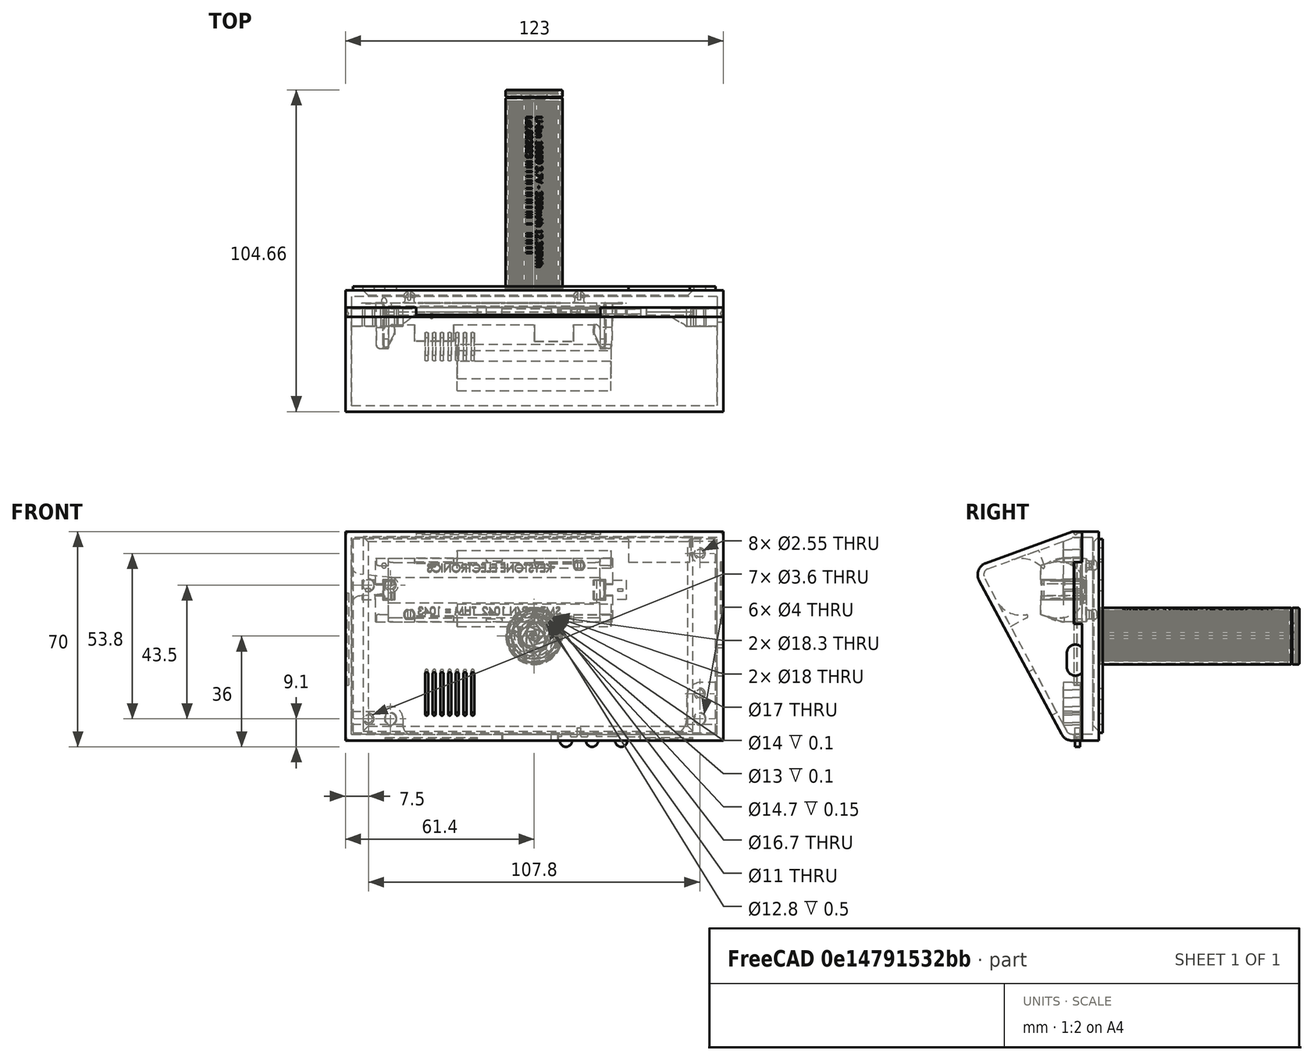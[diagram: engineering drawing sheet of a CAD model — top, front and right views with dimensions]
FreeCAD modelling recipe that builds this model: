
FCSTD DOCUMENT  (FreeCAD 1.0R39285 (Git))
Label: WeatherStation
License: All rights reserved
LicenseURL: https://en.wikipedia.org/wiki/All_rights_reserved
objects: Part::Feature×82, Sketcher::SketchObject×23, PartDesign::Pad×17, PartDesign::Pocket×8, App::Part×3, PartDesign::Body×3, Mesh::Feature×2, Image::ImagePlane×1, PartDesign::SubShapeBinder×1, PartDesign::LinearPattern×1, PartDesign::Fillet×1, PartDesign::Chamfer×1
note: 215 computed .brp shape members not serialized (recipe doc carries the construction recipe); baked Part::Feature solids carry a one-line shape summary decoded from their .brp

FEATURE [Part::Feature] Part__Feature  label="LiLyGO T5-4.7 inch S3 E-paper"
  shape: bbox 118.4 x 6.142 x 63.4 mm, 1563 faces, 0 solids (baked)
FEATURE [Part::Feature] Part__Feature001  label="LiLyGO T5-4.7 inch S3 E-paper001"
  shape: bbox 7.901 x 3.961 x 8.941 mm, 399 faces, 0 solids (baked)
FEATURE [Part::Feature] Part__Feature002  label="LiLyGO T5-4.7 inch S3 E-paper002"
  shape: bbox 10 x 5.45 x 6.416 mm, 158 faces, 0 solids (baked)
FEATURE [Part::Feature] Part__Feature003  label="LiLyGO T5-4.7 inch S3 E-paper003"
  shape: bbox 10 x 5.45 x 6.416 mm, 158 faces, 0 solids (baked)
FEATURE [Part::Feature] Part__Feature004  label="LiLyGO T5-4.7 inch S3 E-paper004"
  shape: bbox 18 x 0.818 x 25.5 mm, 129 faces, 0 solids (baked)
FEATURE [Part::Feature] Part__Feature005  label="LiLyGO T5-4.7 inch S3 E-paper005"
  shape: bbox 15.8 x 2.3 x 17.6 mm, 847 faces, 0 solids (baked)
FEATURE [Part::Feature] Part__Feature006  label="LiLyGO T5-4.7 inch S3 E-paper006"
  shape: bbox 0.9 x 0.018 x 0.9 mm, 6 faces, 0 solids (baked)
FEATURE [Part::Feature] Part__Feature007  label="LiLyGO T5-4.7 inch S3 E-paper007"
  shape: bbox 0.9 x 0.018 x 0.9 mm, 6 faces, 0 solids (baked)
FEATURE [Part::Feature] Part__Feature008  label="LiLyGO T5-4.7 inch S3 E-paper008"
  shape: bbox 0.9 x 0.018 x 0.9 mm, 6 faces, 0 solids (baked)
FEATURE [Part::Feature] Part__Feature009  label="LiLyGO T5-4.7 inch S3 E-paper009"
  shape: bbox 0.9 x 0.018 x 0.9 mm, 6 faces, 0 solids (baked)
FEATURE [Part::Feature] Part__Feature010  label="LiLyGO T5-4.7 inch S3 E-paper010"
  shape: bbox 0.9 x 0.018 x 0.9 mm, 6 faces, 0 solids (baked)
FEATURE [Part::Feature] Part__Feature011  label="LiLyGO T5-4.7 inch S3 E-paper011"
  shape: bbox 0.9 x 0.018 x 0.9 mm, 6 faces, 0 solids (baked)
FEATURE [Part::Feature] Part__Feature012  label="LiLyGO T5-4.7 inch S3 E-paper012"
  shape: bbox 0.9 x 0.018 x 0.9 mm, 6 faces, 0 solids (baked)
FEATURE [Part::Feature] Part__Feature013  label="LiLyGO T5-4.7 inch S3 E-paper013"
  shape: bbox 0.9 x 0.018 x 0.9 mm, 6 faces, 0 solids (baked)
FEATURE [Part::Feature] Part__Feature014  label="LiLyGO T5-4.7 inch S3 E-paper014"
  shape: bbox 0.9 x 0.018 x 0.9 mm, 6 faces, 0 solids (baked)
FEATURE [Part::Feature] Part__Feature015  label="LiLyGO T5-4.7 inch S3 E-paper015"
  shape: bbox 0.868 x 0.836 x 0.9 mm, 16 faces, 0 solids (baked)
FEATURE [Part::Feature] Part__Feature016  label="LiLyGO T5-4.7 inch S3 E-paper016"
  shape: bbox 0.868 x 0.836 x 0.9 mm, 16 faces, 0 solids (baked)
FEATURE [Part::Feature] Part__Feature017  label="LiLyGO T5-4.7 inch S3 E-paper017"
  shape: bbox 0.868 x 0.836 x 0.9 mm, 16 faces, 0 solids (baked)
FEATURE [Part::Feature] Part__Feature018  label="LiLyGO T5-4.7 inch S3 E-paper018"
  shape: bbox 0.868 x 0.836 x 0.9 mm, 16 faces, 0 solids (baked)
FEATURE [Part::Feature] Part__Feature019  label="LiLyGO T5-4.7 inch S3 E-paper019"
  shape: bbox 0.868 x 0.836 x 0.9 mm, 16 faces, 0 solids (baked)
FEATURE [Part::Feature] Part__Feature020  label="LiLyGO T5-4.7 inch S3 E-paper020"
  shape: bbox 0.868 x 0.836 x 0.9 mm, 16 faces, 0 solids (baked)
FEATURE [Part::Feature] Part__Feature021  label="LiLyGO T5-4.7 inch S3 E-paper021"
  shape: bbox 0.868 x 0.836 x 0.9 mm, 16 faces, 0 solids (baked)
FEATURE [Part::Feature] Part__Feature022  label="LiLyGO T5-4.7 inch S3 E-paper022"
  shape: bbox 0.868 x 0.836 x 0.9 mm, 16 faces, 0 solids (baked)
FEATURE [Part::Feature] Part__Feature023  label="LiLyGO T5-4.7 inch S3 E-paper023"
  shape: bbox 0.868 x 0.836 x 0.9 mm, 16 faces, 0 solids (baked)
FEATURE [Part::Feature] Part__Feature024  label="LiLyGO T5-4.7 inch S3 E-paper024"
  shape: bbox 0.868 x 0.836 x 0.9 mm, 16 faces, 0 solids (baked)
FEATURE [Part::Feature] Part__Feature025  label="LiLyGO T5-4.7 inch S3 E-paper025"
  shape: bbox 0.868 x 0.836 x 0.9 mm, 16 faces, 0 solids (baked)
FEATURE [Part::Feature] Part__Feature026  label="LiLyGO T5-4.7 inch S3 E-paper026"
  shape: bbox 0.868 x 0.836 x 0.9 mm, 16 faces, 0 solids (baked)
FEATURE [Part::Feature] Part__Feature027  label="LiLyGO T5-4.7 inch S3 E-paper027"
  shape: bbox 0.868 x 0.836 x 0.9 mm, 16 faces, 0 solids (baked)
FEATURE [Part::Feature] Part__Feature028  label="LiLyGO T5-4.7 inch S3 E-paper028"
  shape: bbox 0.868 x 0.836 x 0.9 mm, 16 faces, 0 solids (baked)
FEATURE [Part::Feature] Part__Feature029  label="LiLyGO T5-4.7 inch S3 E-paper029"
  shape: bbox 0.868 x 0.836 x 0.9 mm, 16 faces, 0 solids (baked)
FEATURE [Part::Feature] Part__Feature030  label="LiLyGO T5-4.7 inch S3 E-paper030"
  shape: bbox 0.868 x 0.836 x 0.9 mm, 16 faces, 0 solids (baked)
FEATURE [Part::Feature] Part__Feature031  label="LiLyGO T5-4.7 inch S3 E-paper031"
  shape: bbox 0.868 x 0.836 x 0.9 mm, 16 faces, 0 solids (baked)
FEATURE [Part::Feature] Part__Feature032  label="LiLyGO T5-4.7 inch S3 E-paper032"
  shape: bbox 0.868 x 0.836 x 0.9 mm, 16 faces, 0 solids (baked)
FEATURE [Part::Feature] Part__Feature033  label="LiLyGO T5-4.7 inch S3 E-paper033"
  shape: bbox 0.868 x 0.836 x 0.9 mm, 16 faces, 0 solids (baked)
FEATURE [Part::Feature] Part__Feature034  label="LiLyGO T5-4.7 inch S3 E-paper034"
  shape: bbox 0.868 x 0.836 x 0.9 mm, 16 faces, 0 solids (baked)
FEATURE [Part::Feature] Part__Feature035  label="LiLyGO T5-4.7 inch S3 E-paper035"
  shape: bbox 0.868 x 0.836 x 0.9 mm, 16 faces, 0 solids (baked)
FEATURE [Part::Feature] Part__Feature036  label="LiLyGO T5-4.7 inch S3 E-paper036"
  shape: bbox 0.868 x 0.836 x 0.9 mm, 16 faces, 0 solids (baked)
FEATURE [Part::Feature] Part__Feature037  label="LiLyGO T5-4.7 inch S3 E-paper037"
  shape: bbox 0.868 x 0.836 x 0.9 mm, 16 faces, 0 solids (baked)
FEATURE [Part::Feature] Part__Feature038  label="LiLyGO T5-4.7 inch S3 E-paper038"
  shape: bbox 0.868 x 0.836 x 0.9 mm, 16 faces, 0 solids (baked)
FEATURE [Part::Feature] Part__Feature039  label="LiLyGO T5-4.7 inch S3 E-paper039"
  shape: bbox 0.868 x 0.836 x 0.9 mm, 16 faces, 0 solids (baked)
FEATURE [Part::Feature] Part__Feature040  label="LiLyGO T5-4.7 inch S3 E-paper040"
  shape: bbox 0.868 x 0.836 x 0.9 mm, 16 faces, 0 solids (baked)
FEATURE [Part::Feature] Part__Feature041  label="LiLyGO T5-4.7 inch S3 E-paper041"
  shape: bbox 0.868 x 0.836 x 0.9 mm, 16 faces, 0 solids (baked)
FEATURE [Part::Feature] Part__Feature042  label="LiLyGO T5-4.7 inch S3 E-paper042"
  shape: bbox 0.868 x 0.836 x 0.9 mm, 16 faces, 0 solids (baked)
FEATURE [Part::Feature] Part__Feature043  label="LiLyGO T5-4.7 inch S3 E-paper043"
  shape: bbox 0.9 x 0.836 x 0.868 mm, 16 faces, 0 solids (baked)
FEATURE [Part::Feature] Part__Feature044  label="LiLyGO T5-4.7 inch S3 E-paper044"
  shape: bbox 0.9 x 0.836 x 0.868 mm, 16 faces, 0 solids (baked)
FEATURE [Part::Feature] Part__Feature045  label="LiLyGO T5-4.7 inch S3 E-paper045"
  shape: bbox 0.9 x 0.836 x 0.868 mm, 16 faces, 0 solids (baked)
FEATURE [Part::Feature] Part__Feature046  label="LiLyGO T5-4.7 inch S3 E-paper046"
  shape: bbox 0.9 x 0.836 x 0.868 mm, 16 faces, 0 solids (baked)
FEATURE [Part::Feature] Part__Feature047  label="LiLyGO T5-4.7 inch S3 E-paper047"
  shape: bbox 0.9 x 0.836 x 0.868 mm, 16 faces, 0 solids (baked)
FEATURE [Part::Feature] Part__Feature048  label="LiLyGO T5-4.7 inch S3 E-paper048"
  shape: bbox 0.9 x 0.836 x 0.868 mm, 16 faces, 0 solids (baked)
FEATURE [Part::Feature] Part__Feature049  label="LiLyGO T5-4.7 inch S3 E-paper049"
  shape: bbox 0.9 x 0.836 x 0.868 mm, 16 faces, 0 solids (baked)
FEATURE [Part::Feature] Part__Feature050  label="LiLyGO T5-4.7 inch S3 E-paper050"
  shape: bbox 0.9 x 0.836 x 0.868 mm, 16 faces, 0 solids (baked)
FEATURE [Part::Feature] Part__Feature051  label="LiLyGO T5-4.7 inch S3 E-paper051"
  shape: bbox 0.9 x 0.836 x 0.868 mm, 16 faces, 0 solids (baked)
FEATURE [Part::Feature] Part__Feature052  label="LiLyGO T5-4.7 inch S3 E-paper052"
  shape: bbox 0.9 x 0.836 x 0.868 mm, 16 faces, 0 solids (baked)
FEATURE [Part::Feature] Part__Feature053  label="LiLyGO T5-4.7 inch S3 E-paper053"
  shape: bbox 0.9 x 0.836 x 0.868 mm, 16 faces, 0 solids (baked)
FEATURE [Part::Feature] Part__Feature054  label="LiLyGO T5-4.7 inch S3 E-paper054"
  shape: bbox 0.9 x 0.836 x 0.868 mm, 16 faces, 0 solids (baked)
FEATURE [Part::Feature] Part__Feature055  label="LiLyGO T5-4.7 inch S3 E-paper055"
  shape: bbox 0.8 x 1.034 x 8.828 mm, 98 faces, 0 solids (baked)
FEATURE [Part::Feature] Part__Feature056  label="LiLyGO T5-4.7 inch S3 E-paper056"
  shape: bbox 0.8 x 1.034 x 9.125 mm, 98 faces, 0 solids (baked)
FEATURE [Part::Feature] Part__Feature057  label="LiLyGO T5-4.7 inch S3 E-paper057"
  shape: bbox 0.8 x 1.034 x 8.828 mm, 98 faces, 0 solids (baked)
FEATURE [Part::Feature] Part__Feature058  label="LiLyGO T5-4.7 inch S3 E-paper058"
  shape: bbox 0.8 x 1.053 x 8.525 mm, 98 faces, 0 solids (baked)
FEATURE [Part::Feature] Part__Feature059  label="LiLyGO T5-4.7 inch S3 E-paper059"
  shape: bbox 0.8 x 1.034 x 8.828 mm, 98 faces, 0 solids (baked)
FEATURE [Part::Feature] Part__Feature060  label="LiLyGO T5-4.7 inch S3 E-paper060"
  shape: bbox 0.8 x 1.053 x 8.525 mm, 98 faces, 0 solids (baked)
FEATURE [Part::Feature] Part__Feature061  label="LiLyGO T5-4.7 inch S3 E-paper061"
  shape: bbox 0.8 x 1.034 x 8.828 mm, 98 faces, 0 solids (baked)
FEATURE [Part::Feature] Part__Feature062  label="LiLyGO T5-4.7 inch S3 E-paper062"
  shape: bbox 0.8 x 1.034 x 8.828 mm, 98 faces, 0 solids (baked)
FEATURE [Part::Feature] Part__Feature063  label="LiLyGO T5-4.7 inch S3 E-paper063"
  shape: bbox 4.48 x 1.155 x 14 mm, 148 faces, 0 solids (baked)
FEATURE [Part::Feature] Part__Feature064  label="LiLyGO T5-4.7 inch S3 E-paper064"
  shape: bbox 14.24 x 1.381 x 14.95 mm, 295 faces, 0 solids (baked)
FEATURE [Part::Feature] Part__Feature065  label="LiLyGO T5-4.7 inch S3 E-paper065"
  shape: bbox 2.66 x 1.087 x 9.021 mm, 113 faces, 0 solids (baked)
FEATURE [Part::Feature] Part__Feature066  label="LiLyGO T5-4.7 inch S3 E-paper066"
  shape: bbox 0.5151 x 0.833 x 6.833 mm, 16 faces, 0 solids (baked)
FEATURE [Part::Feature] Part__Feature067  label="LiLyGO T5-4.7 inch S3 E-paper067"
  shape: bbox 14.94 x 1.5 x 14.95 mm, 496 faces, 0 solids (baked)
FEATURE [Part::Feature] Part__Feature068  label="LiLyGO T5-4.7 inch S3 E-paper068"
  shape: bbox 7.5 x 9.25 x 11.5 mm, 87 faces, 0 solids (baked)
FEATURE [Part::Feature] Part__Feature069  label="LiLyGO T5-4.7 inch S3 E-paper069"
  shape: bbox 1.44 x 1.308 x 10.41 mm, 3 faces, 0 solids (baked)
FEATURE [Sketcher::SketchObject] Sketch
  ArcFitTolerance = 1e-06
  AttachmentSupport = -> [XZ_Plane002]
  FullyConstrained = true
  MakeInternals = false
  MapMode = 5
  Placement = pos=(0,0,0) rot=(1,0,0;1.5708rad)
  expr: Constraints[16] = 119 + 2 + 2
  expr: Constraints[17] = 64 + 2 + 2
  sketch-geometry (8):
    g0: LineSegment StartX=61.6 StartY=34 StartZ=0 EndX=-61.4 EndY=34 EndZ=0
    g1: LineSegment StartX=-61.4 StartY=34 StartZ=0 EndX=-61.4 EndY=-34 EndZ=0
    g2: LineSegment StartX=-61.4 StartY=-34 StartZ=0 EndX=61.6 EndY=-34 EndZ=0
    g3: LineSegment StartX=61.6 StartY=-34 StartZ=0 EndX=61.6 EndY=34 EndZ=0
    g4: LineSegment StartX=-54 StartY=-29.3 StartZ=0 EndX=50 EndY=-29.3 EndZ=0
    g5: LineSegment StartX=50 StartY=-29.3 StartZ=0 EndX=50 EndY=30.7 EndZ=0
    g6: LineSegment StartX=50 StartY=30.7 StartZ=0 EndX=-54 EndY=30.7 EndZ=0
    g7: LineSegment StartX=-54 StartY=30.7 StartZ=0 EndX=-54 EndY=-29.3 EndZ=0
  constraints (24):
    c: Coincident(g0,g1)
    c: Coincident(g1,g2)
    c: Coincident(g2,g3)
    c: Coincident(g3,g0)
    c: Horizontal(g0)
    c: Horizontal(g2)
    c: Vertical(g1)
    c: Vertical(g3)
    c: Coincident(g4,g5)
    c: Coincident(g5,g6)
    c: Coincident(g6,g7)
    c: Coincident(g7,g4)
    c: Horizontal(g4)
    c: Horizontal(g6)
    c: Vertical(g5)
    c: Vertical(g7)
    c: DistanceX(g2,g2) = 123
    c: DistanceY(g3,g3) = 68
    c: Distance(g1,g-2) = 61.4
    c: Distance(g-1,g2) = 34
    c: DistanceX(g6,g6) = 104
    c: DistanceY(g5,g5) = 60
    c: DistanceY(g4,g-1) = 29.3
    c: Distance(g4,g-2) = 54
FEATURE [PartDesign::Pad] Pad  label="BeselPad"
  Direction = (0,-1,2e-16)
  Length = 2
  Length2 = 10
  Placement = pos=(0,0,0) rot=(1,0,0;1.5708rad)
  Profile = -> Sketch
  ReferenceAxis = -> Sketch [N_Axis]
  Suppressed = false
  Type = 0
FEATURE [Sketcher::SketchObject] Sketch001
  ArcFitTolerance = 1e-06
  AttachmentSupport = -> [Pad]
  ExternalGeometry = -> [Pad]
  FullyConstrained = true
  MakeInternals = false
  MapMode = 5
  Placement = pos=(0,-2,4e-16) rot=(1,0,0;1.5708rad)
  sketch-geometry (8):
    g0: LineSegment StartX=-61.4 StartY=34 StartZ=0 EndX=-61.4 EndY=-34 EndZ=0
    g1: LineSegment StartX=-61.4 StartY=-34 StartZ=0 EndX=61.6 EndY=-34 EndZ=0
    g2: LineSegment StartX=61.6 StartY=-34 StartZ=0 EndX=61.6 EndY=34 EndZ=0
    g3: LineSegment StartX=61.6 StartY=34 StartZ=0 EndX=-61.4 EndY=34 EndZ=0
    g4: LineSegment StartX=-59.4 StartY=32 StartZ=0 EndX=-59.4 EndY=-32 EndZ=0
    g5: LineSegment StartX=-59.4 StartY=-32 StartZ=0 EndX=59.6 EndY=-32 EndZ=0
    g6: LineSegment StartX=59.6 StartY=-32 StartZ=0 EndX=59.6 EndY=32 EndZ=0
    g7: LineSegment StartX=59.6 StartY=32 StartZ=0 EndX=-59.4 EndY=32 EndZ=0
  constraints (22):
    c: Coincident(g0,g1)
    c: Coincident(g1,g2)
    c: Coincident(g2,g3)
    c: Coincident(g3,g0)
    c: Vertical(g0)
    c: Vertical(g2)
    c: Horizontal(g1)
    c: Horizontal(g3)
    c: Coincident(g0,g-3)
    c: Coincident(g1,g-4)
    c: Coincident(g4,g5)
    c: Coincident(g5,g6)
    c: Coincident(g6,g7)
    c: Coincident(g7,g4)
    c: Vertical(g4)
    c: Vertical(g6)
    c: Horizontal(g5)
    c: Horizontal(g7)
    c: DistanceY(g4,g4) = 64
    c: DistanceX(g5,g5) = 119
    c: Distance(g4,g0) = 2
    c: Distance(g4,g3) = 2
FEATURE [PartDesign::Pad] Pad001  label="SideWallPad"
  BaseFeature = -> Pad
  Direction = (0,-1,2e-16)
  Length = 3.5
  Length2 = 10
  Placement = pos=(0,0,0) rot=(1,0,0;1.5708rad)
  Profile = -> Sketch001
  ReferenceAxis = -> Sketch001 [N_Axis]
  Suppressed = false
  Type = 0
FEATURE [Part::Feature] Part__Feature070  label="Li-Ion_18650_cell"
  shape: bbox 19.81 x 65.04 x 19.81 mm, 31 faces (baked)
FEATURE [Part::Feature] Part__Feature071  label="Li-Ion_18650_cell001"
  shape: bbox 17.9 x 0.5 x 17.9 mm, 4 faces (baked)
FEATURE [Part::Feature] Part__Feature072  label="Li-Ion_18650_cell002"
  shape: bbox 17.52 x 3.32 x 17.52 mm, 44 faces (baked)
FEATURE [Part::Feature] Part__Feature073  label="Li-Ion_18650_cell003"
  shape: bbox 16.4 x 61 x 16.35 mm, 6 faces (baked)
FEATURE [Part::Feature] Part__Feature074  label="Li-Ion_18650_cell004"
  shape: bbox 16.7 x 61 x 16.66 mm, 6 faces (baked)
FEATURE [Part::Feature] Part__Feature075  label="Li-Ion_18650_cell005"
  shape: bbox 17.01 x 61 x 16.97 mm, 6 faces (baked)
FEATURE [Part::Feature] Part__Feature076  label="Li-Ion_18650_cell006"
  shape: bbox 17.13 x 0.2387 x 17.13 mm, 3 faces (baked)
FEATURE [Part::Feature] Part__Feature077  label="Li-Ion_18650_cell007"
  shape: bbox 16.02 x 0.1534 x 16.02 mm, 3 faces (baked)
FEATURE [Part::Feature] Part__Feature078  label="Li-Ion_18650_cell008"
  shape: bbox 17.91 x 61.47 x 17.91 mm, 4 faces (baked)
FEATURE [Part::Feature] Part__Feature079  label="Li-Ion_18650_cell009"
  shape: bbox 17.7 x 0.1 x 17.7 mm, 4 faces (baked)
FEATURE [Part::Feature] Part__Feature080  label="Li-Ion_18650_cell010"
  shape: bbox 20.03 x 65.36 x 141.7 mm, 778 faces (baked)
FEATURE [App::Part] Li_Ion_18650_cell  label="Li-Ion_18650_cell011"
  Group = -> [Part__Feature070,Part__Feature071,Part__Feature072,Part__Feature073,Part__Feature074,Part__Feature075,Part__Feature076,Part__Feature077,Part__Feature078,Part__Feature079,Part__Feature080]
  Origin = -> Origin004
  Placement = pos=(-32.5,-18.75,15.75) rot=(0,0,1;4.71239rad)
FEATURE [Part::Feature] Part__Feature081  label="keystone-PN1042"
  Placement = pos=(-13,-4,15) rot=(-0.707107,0,0.707107;3.14159rad)
  shape: bbox 86.01 x 18.29 x 20.82 mm, 683 faces (baked)
FEATURE [Mesh::Feature] a  label="RefShell_back"
  Placement = pos=(-9e-16,7.25,0) rot=(1,0,0;3.14159rad)
FEATURE [Image::ImagePlane] LILYGO_T5_E_PAPER_1  label="LILYGO-T5-E-PAPER_1"
  Placement = pos=(0,0,0) rot=(1,0,0;1.5708rad)
  XSize = 163.006
  YSize = 89.7063
FEATURE [Sketcher::SketchObject] Sketch007
  ArcFitTolerance = 1e-06
  AttachmentSupport = -> [XZ_Plane005]
  FullyConstrained = true
  MakeInternals = false
  MapMode = 5
  Placement = pos=(0,0,0) rot=(1,0,0;1.5708rad)
  sketch-geometry (15):
    g0: LineSegment StartX=-59 StartY=31.5 StartZ=0 EndX=-59 EndY=-31.5 EndZ=0
    g1: LineSegment StartX=-59 StartY=-31.5 StartZ=0 EndX=59 EndY=-31.5 EndZ=0
    g2: LineSegment StartX=59 StartY=-31.5 StartZ=0 EndX=59 EndY=31.5 EndZ=0
    g3: LineSegment StartX=59 StartY=31.5 StartZ=0 EndX=50.7 EndY=31.5 EndZ=0
    g4: LineSegment StartX=30.7 StartY=31.5 StartZ=0 EndX=30.7 EndY=24.1 EndZ=0
    g5: LineSegment StartX=30.7 StartY=24.1 StartZ=0 EndX=50.7 EndY=24.1 EndZ=0
    g6: LineSegment StartX=50.7 StartY=24.1 StartZ=0 EndX=50.7 EndY=31.5 EndZ=0
    g7: LineSegment StartX=30.7 StartY=31.5 StartZ=0 EndX=-59 EndY=31.5 EndZ=0
    g8: Circle CenterX=53.9 CenterY=26.9 CenterZ=0 NormalX=0 NormalY=0 NormalZ=1 AngleXU=0 Radius=1.8
    g9: Circle CenterX=53.9 CenterY=-18.7 CenterZ=0 NormalX=0 NormalY=0 NormalZ=1 AngleXU=0 Radius=1.8
    g10: Circle CenterX=53.9 CenterY=-26.9 CenterZ=0 NormalX=0 NormalY=0 NormalZ=1 AngleXU=0 Radius=1.8
    g11: Circle CenterX=-53.9 CenterY=-26.9 CenterZ=0 NormalX=0 NormalY=0 NormalZ=1 AngleXU=0 Radius=1.8
    g12: Circle CenterX=-46.7 CenterY=-26.9 CenterZ=0 NormalX=0 NormalY=0 NormalZ=1 AngleXU=0 Radius=1.8
    g13: Circle CenterX=-53.9 CenterY=16.6 CenterZ=0 NormalX=0 NormalY=0 NormalZ=1 AngleXU=0 Radius=1.8
    g14: Circle CenterX=-46.7 CenterY=16.6 CenterZ=0 NormalX=0 NormalY=0 NormalZ=1 AngleXU=0 Radius=1.8
  constraints (45):
    c: Coincident(g0,g1)
    c: Coincident(g1,g2)
    c: Coincident(g2,g3)
    c: Coincident(g7,g0)
    c: Vertical(g0)
    c: Vertical(g2)
    c: Horizontal(g1)
    c: Horizontal(g3)
    c: Distance(g0,g2) = 118
    c: Distance(g1,g7) = 63
    c: DistanceY(g-1,g2) = 31.5
    c: DistanceX(g-1,g2) = 59
    c: Coincident(g4,g5)
    c: Coincident(g5,g6)
    c: Horizontal(g5)
    c: Vertical(g4)
    c: Vertical(g6)
    c: Horizontal(g4,g3)
    c: DistanceY(g4,g4) = 7.4
    c: DistanceX(g5,g5) = 20
    c: DistanceX(g3,g3) = 8.3
    c: Coincident(g6,g3)
    c: Horizontal(g7)
    c: Coincident(g4,g7)
    c: Equal(g13,g14)
    c: Equal(g14,g11)
    c: Equal(g11,g12)
    c: Equal(g12,g10)
    c: Equal(g10,g9)
    c: Equal(g9,g8)
    c: Diameter(g8) = 3.6
    c: Horizontal(g13,g14)
    c: Horizontal(g11,g12)
    c: Horizontal(g12,g10)
    c: Vertical(g8,g9)
    c: Vertical(g9,g10)
    c: Distance(g11,g1) = 2.8
    c: Distance(g11,g0) = 3.3
    c: Vertical(g11,g13)
    c: Vertical(g12,g14)
    c: Distance(g12,g0) = 10.5
    c: Distance(g13,g7) = 13.1
    c: Distance(g10,g2) = 3.3
    c: Distance(g9,g1) = 11
    c: Distance(g8,g3) = 2.8
FEATURE [PartDesign::Pad] Pad005
  Direction = (0,-1,2e-16)
  Length = 1.2
  Length2 = 10
  Placement = pos=(0,0,0) rot=(1,0,0;1.5708rad)
  Profile = -> Sketch007
  ReferenceAxis = -> Sketch007 [N_Axis]
  Suppressed = false
  Type = 0
FEATURE [PartDesign::Body] Body002  label="PCB"
  AllowCompound = false
  Group = -> [Sketch007,Pad005]
  Origin = -> Origin005
  Placement = pos=(0,1.25,0) rot=(0,0,1;0rad)
  Tip = -> Pad005
FEATURE [App::Part] LiLyGO_T5_4_7_inch_S3_E_paper  label="LiLyGO T5-4.7 inch S3 E-paper070"
  Group = -> [Part__Feature,Part__Feature001,Part__Feature002,Part__Feature003,Part__Feature004,Part__Feature005,Part__Feature006,Part__Feature007,Part__Feature008,Part__Feature009,Part__Feature010,Part__Feature011,Part__Feature012,Part__Feature013,Part__Feature014,Part__Feature015,Part__Feature016,Part__Feature017,Part__Feature018,Part__Feature019,Part__Feature020,Part__Feature021,Part__Feature022,+49 more]
  Origin = -> Origin
FEATURE [Mesh::Feature] b
  Placement = pos=(0,7.25,-9e-16) rot=(1,0,0;3.14159rad)
FEATURE [Sketcher::SketchObject] Sketch008
  ArcFitTolerance = 1e-06
  AttachmentSupport = -> [Pad001]
  ExternalGeometry = -> [Pad001]
  FullyConstrained = true
  MakeInternals = false
  MapMode = 5
  Placement = pos=(61.6,0,0) rot=(0.707107,0,0.707107;3.14159rad)
  sketch-geometry (5):
    g0: LineSegment StartX=34 StartY=5.5 StartZ=0 EndX=34 EndY=8 EndZ=0
    g1: LineSegment StartX=33.5 StartY=5.5 StartZ=0 EndX=33.5 EndY=7 EndZ=0
    g2: ArcOfCircle CenterX=33.5 CenterY=7.5 CenterZ=0 NormalX=0 NormalY=0 NormalZ=1 AngleXU=0 Radius=0.5 StartAngle=1.5708 EndAngle=4.71239
    g3: LineSegment StartX=33.5 StartY=8 StartZ=0 EndX=34 EndY=8 EndZ=0
    g4: LineSegment StartX=33.5 StartY=5.5 StartZ=0 EndX=34 EndY=5.5 EndZ=0
  constraints (15):
    c: Coincident(g0,g-4)
    c: Vertical(g0)
    c: PointOnObject(g1,g-7)
    c: Vertical(g1)
    c: Coincident(g2,g1)
    c: Coincident(g3,g2)
    c: Coincident(g3,g0)
    c: Horizontal(g3)
    c: Radius(g2) = 0.5
    c: Distance(g3,g3) = 0.5
    c: DistanceY(g0,g0) = 2.5
    c: Vertical(g1,g2)
    c: Vertical(g2,g2)
    c: Coincident(g4,g1)
    c: Coincident(g4,g0)
FEATURE [PartDesign::Pad] Pad006  label="BotTabPad"
  BaseFeature = -> Pad001
  Direction = (1,0,-2e-16)
  Length = 100
  Length2 = -40
  Placement = pos=(0,0,0) rot=(1,0,0;1.5708rad)
  Profile = -> Sketch008
  ReferenceAxis = -> Sketch008 [N_Axis]
  Reversed = true
  Suppressed = false
  Type = 4
FEATURE [Sketcher::SketchObject] Sketch009
  ArcFitTolerance = 1e-06
  AttachmentSupport = -> [Pad006]
  ExternalGeometry = -> [Pad006]
  FullyConstrained = true
  MakeInternals = false
  MapMode = 5
  Placement = pos=(0,1.5e-14,34) rot=(0,0,1;3.14159rad)
  sketch-geometry (5):
    g0: LineSegment StartX=-61.1 StartY=5.5 StartZ=0 EndX=-61.6 EndY=5.5 EndZ=0
    g1: LineSegment StartX=-61.6 StartY=5.5 StartZ=0 EndX=-61.6 EndY=8 EndZ=0
    g2: LineSegment StartX=-61.6 StartY=8 StartZ=0 EndX=-61.1 EndY=8 EndZ=0
    g3: LineSegment StartX=-61.1 StartY=5.5 StartZ=0 EndX=-61.1 EndY=7 EndZ=0
    g4: ArcOfCircle CenterX=-61.1 CenterY=7.5 CenterZ=0 NormalX=0 NormalY=0 NormalZ=1 AngleXU=0 Radius=0.5 StartAngle=4.71239 EndAngle=7.85398
  constraints (15):
    c: PointOnObject(g0,g-3)
    c: Coincident(g0,g-3)
    c: Coincident(g1,g0)
    c: Vertical(g1)
    c: Coincident(g2,g1)
    c: Horizontal(g2)
    c: Coincident(g3,g0)
    c: Vertical(g3)
    c: Coincident(g4,g3)
    c: Coincident(g4,g2)
    c: Vertical(g2,g4)
    c: Vertical(g4,g3)
    c: DistanceX(g2,g2) = 0.5
    c: Radius(g4) = 0.5
    c: DistanceY(g1,g1) = 2.5
FEATURE [PartDesign::Pad] Pad007  label="RightTabPad"
  BaseFeature = -> Pad006
  Direction = (0,0,1)
  Length = 30
  Length2 = -10
  Placement = pos=(0,0,0) rot=(1,0,0;1.5708rad)
  Profile = -> Sketch009
  ReferenceAxis = -> Sketch009 [N_Axis]
  Reversed = true
  Suppressed = false
  Type = 4
FEATURE [Sketcher::SketchObject] Sketch010
  ArcFitTolerance = 1e-06
  AttachmentSupport = -> [Pad007]
  ExternalGeometry = -> [Pad007]
  FullyConstrained = true
  MakeInternals = false
  MapMode = 5
  Placement = pos=(0,1.5e-14,34) rot=(0,0,1;3.14159rad)
  sketch-geometry (5):
    g0: LineSegment StartX=60.9 StartY=7 StartZ=0 EndX=60.9 EndY=5.5 EndZ=0
    g1: LineSegment StartX=60.9 StartY=5.5 StartZ=0 EndX=61.4 EndY=5.5 EndZ=0
    g2: LineSegment StartX=61.4 StartY=5.5 StartZ=0 EndX=61.4 EndY=8 EndZ=0
    g3: LineSegment StartX=61.4 StartY=8 StartZ=0 EndX=60.9 EndY=8 EndZ=0
    g4: ArcOfCircle CenterX=60.9 CenterY=7.5 CenterZ=0 NormalX=0 NormalY=0 NormalZ=1 AngleXU=0 Radius=0.5 StartAngle=1.5708 EndAngle=4.71239
  constraints (15):
    c: PointOnObject(g0,g-4)
    c: Vertical(g0)
    c: Coincident(g0,g1)
    c: Coincident(g1,g-4)
    c: Coincident(g1,g2)
    c: Vertical(g2)
    c: Coincident(g2,g3)
    c: Horizontal(g3)
    c: Coincident(g4,g0)
    c: Coincident(g4,g3)
    c: DistanceX(g3,g3) = 0.5
    c: Vertical(g4,g3)
    c: Vertical(g3,g0)
    c: Radius(g4) = 0.5
    c: DistanceY(g2,g2) = 2.5
FEATURE [PartDesign::Pad] Pad008  label="LeftTabPad"
  BaseFeature = -> Pad007
  Direction = (0,0,1)
  Length = 50
  Length2 = -20
  Placement = pos=(0,0,0) rot=(1,0,0;1.5708rad)
  Profile = -> Sketch010
  ReferenceAxis = -> Sketch010 [N_Axis]
  Reversed = true
  Suppressed = false
  Type = 4
FEATURE [Sketcher::SketchObject] Sketch011
  ArcFitTolerance = 1e-06
  AttachmentSupport = -> [Pad008]
  ExternalGeometry = -> [Pad008]
  FullyConstrained = true
  MakeInternals = false
  MapMode = 5
  Placement = pos=(61.6,0,0) rot=(0.707107,0,0.707107;3.14159rad)
  sketch-geometry (5):
    g0: LineSegment StartX=-33.5 StartY=7 StartZ=0 EndX=-33.5 EndY=5.5 EndZ=0
    g1: LineSegment StartX=-33.5 StartY=5.5 StartZ=0 EndX=-34 EndY=5.5 EndZ=0
    g2: LineSegment StartX=-34 StartY=5.5 StartZ=0 EndX=-34 EndY=8 EndZ=0
    g3: LineSegment StartX=-34 StartY=8 StartZ=0 EndX=-33.5 EndY=8 EndZ=0
    g4: ArcOfCircle CenterX=-33.5 CenterY=7.5 CenterZ=0 NormalX=0 NormalY=0 NormalZ=1 AngleXU=0 Radius=0.5 StartAngle=4.71239 EndAngle=7.85398
  constraints (15):
    c: PointOnObject(g0,g-3)
    c: Vertical(g0)
    c: Coincident(g0,g1)
    c: Coincident(g1,g-3)
    c: Coincident(g1,g2)
    c: Vertical(g2)
    c: Coincident(g2,g3)
    c: Horizontal(g3)
    c: Coincident(g4,g3)
    c: Coincident(g4,g0)
    c: DistanceX(g3,g3) = 0.5
    c: Radius(g4) = 0.5
    c: DistanceY(g2,g2) = 2.5
    c: Vertical(g0,g4)
    c: Vertical(g4,g3)
FEATURE [PartDesign::Pad] Pad009  label="Top1TabPad"
  BaseFeature = -> Pad008
  Direction = (1,0,-2e-16)
  Length = 25
  Length2 = -10
  Placement = pos=(0,0,0) rot=(1,0,0;1.5708rad)
  Profile = -> Sketch011
  ReferenceAxis = -> Sketch011 [N_Axis]
  Reversed = true
  Suppressed = false
  Type = 4
FEATURE [PartDesign::Pad] Pad010  label="Top2TabPad"
  BaseFeature = -> Pad009
  Direction = (1,0,-2e-16)
  Length = 110
  Length2 = -80
  Placement = pos=(0,0,0) rot=(1,0,0;1.5708rad)
  Profile = -> Sketch011
  ReferenceAxis = -> Sketch011 [N_Axis]
  Reversed = true
  Suppressed = false
  Type = 4
FEATURE [PartDesign::SubShapeBinder] Binder
  BindCopyOnChange = 0
  BindMode = 0
  ClaimChildren = false
  Context = -> Part [Body003.Binder.]
  Fuse = false
  MakeFace = true
  OffsetFill = false
  OffsetIntersection = false
  OffsetJoinType = 0
  OffsetOpenResult = false
  PartialLoad = false
  Relative = true
  Support = -> [Body[Pad010.Face13]]
  _Version = 2
FEATURE [Sketcher::SketchObject] Sketch012
  ArcFitTolerance = 1e-06
  AttachmentSupport = -> [Binder]
  ExternalGeometry = -> [Binder]
  FullyConstrained = true
  MakeInternals = false
  MapMode = 5
  Placement = pos=(0,-5.5,0) rot=(1,0,0;1.5708rad)
  sketch-geometry (32):
    g0: LineSegment StartX=-59.4 StartY=32 StartZ=0 EndX=-59.4 EndY=-32 EndZ=0
    g1: LineSegment StartX=-59.4 StartY=-32 StartZ=0 EndX=7.6 EndY=-32 EndZ=0
    g2: LineSegment StartX=59.6 StartY=-32 StartZ=0 EndX=59.6 EndY=32 EndZ=0
    g3: LineSegment StartX=59.6 StartY=32 StartZ=0 EndX=-59.4 EndY=32 EndZ=0
    g4: LineSegment StartX=-61.4 StartY=34 StartZ=0 EndX=-38.4 EndY=34 EndZ=0
    g5: LineSegment StartX=-38.4 StartY=34 StartZ=0 EndX=-38.4 EndY=33.5 EndZ=0
    g6: LineSegment StartX=-38.4 StartY=33.5 StartZ=0 EndX=21.6 EndY=33.5 EndZ=0
    g7: LineSegment StartX=21.6 StartY=33.5 StartZ=0 EndX=21.6 EndY=34 EndZ=0
    g8: LineSegment StartX=21.6 StartY=34 StartZ=0 EndX=61.6 EndY=34 EndZ=0
    g9: LineSegment StartX=61.6 StartY=34 StartZ=0 EndX=61.6 EndY=24 EndZ=0
    g10: LineSegment StartX=61.6 StartY=24 StartZ=0 EndX=61.1 EndY=24 EndZ=0
    g11: LineSegment StartX=61.1 StartY=24 StartZ=0 EndX=61.1 EndY=4 EndZ=0
    g12: LineSegment StartX=61.1 StartY=4 StartZ=0 EndX=61.6 EndY=4 EndZ=0
    g13: LineSegment StartX=61.6 StartY=-34 StartZ=0 EndX=51.6 EndY=-34 EndZ=0
    g14: LineSegment StartX=51.6 StartY=-34 StartZ=0 EndX=51.6 EndY=-33.5 EndZ=0
    g15: LineSegment StartX=51.6 StartY=-33.5 StartZ=0 EndX=36.6 EndY=-33.5 EndZ=0
    g16: LineSegment StartX=36.6 StartY=-33.5 StartZ=0 EndX=36.6 EndY=-34 EndZ=0
    g17: LineSegment StartX=-18.4 StartY=-34 StartZ=0 EndX=-18.4 EndY=-33.5 EndZ=0
    g18: LineSegment StartX=-18.4 StartY=-33.5 StartZ=0 EndX=-48.4 EndY=-33.5 EndZ=0
    g19: LineSegment StartX=-48.4 StartY=-33.5 StartZ=0 EndX=-48.4 EndY=-34 EndZ=0
    g20: LineSegment StartX=-48.4 StartY=-34 StartZ=0 EndX=-61.4 EndY=-34 EndZ=0
    g21: LineSegment StartX=-61.4 StartY=-34 StartZ=0 EndX=-61.4 EndY=-16 EndZ=0
    g22: LineSegment StartX=-61.4 StartY=-16 StartZ=0 EndX=-60.9 EndY=-16 EndZ=0
    g23: LineSegment StartX=-60.9 StartY=-16 StartZ=0 EndX=-60.9 EndY=14 EndZ=0
    g24: LineSegment StartX=-60.9 StartY=14 StartZ=0 EndX=-61.4 EndY=14 EndZ=0
    g25: LineSegment StartX=-61.4 StartY=14 StartZ=0 EndX=-61.4 EndY=34 EndZ=0
    g26: LineSegment StartX=61.6 StartY=4 StartZ=0 EndX=61.6 EndY=-34 EndZ=0
    g27: LineSegment StartX=7.6 StartY=-32 StartZ=0 EndX=7.6 EndY=-34 EndZ=0
    g28: LineSegment StartX=34.6 StartY=-34 StartZ=0 EndX=34.6 EndY=-32 EndZ=0
    g29: LineSegment StartX=7.6 StartY=-34 StartZ=0 EndX=-18.4 EndY=-34 EndZ=0
    g30: LineSegment StartX=34.6 StartY=-32 StartZ=0 EndX=59.6 EndY=-32 EndZ=0
    g31: LineSegment StartX=36.6 StartY=-34 StartZ=0 EndX=34.6 EndY=-34 EndZ=0
  constraints (71):
    c: Coincident(g0,g1)
    c: Coincident(g30,g2)
    c: Coincident(g3,g0)
    c: Vertical(g0)
    c: Vertical(g2)
    c: Horizontal(g3)
    c: Coincident(g0,g-3)
    c: Coincident(g30,g-4)
    c: Coincident(g-6,g4)
    c: Coincident(g4,g-5)
    c: Coincident(g4,g5)
    c: Coincident(g5,g-18)
    c: Coincident(g5,g6)
    c: Coincident(g6,g-18)
    c: Coincident(g6,g7)
    c: Coincident(g7,g-17)
    c: Coincident(g7,g8)
    c: Coincident(g8,g-17)
    c: Coincident(g8,g9)
    c: Coincident(g9,g-16)
    c: Coincident(g9,g10)
    c: Coincident(g10,g-15)
    c: Coincident(g10,g11)
    c: Coincident(g11,g-15)
    c: Coincident(g11,g12)
    c: Coincident(g12,g-14)
    c: Coincident(g26,g-14)
    c: Coincident(g26,g13)
    c: Coincident(g13,g-13)
    c: Coincident(g13,g14)
    c: Coincident(g14,g-12)
    c: Coincident(g14,g15)
    c: Coincident(g15,g-12)
    c: Coincident(g15,g16)
    c: Coincident(g16,g-11)
    c: Coincident(g29,g-11)
    c: Coincident(g29,g17)
    c: Coincident(g17,g-10)
    c: Coincident(g17,g18)
    c: Coincident(g18,g-10)
    c: Coincident(g18,g19)
    c: Coincident(g19,g-9)
    c: Coincident(g19,g20)
    c: Coincident(g20,g-9)
    c: Coincident(g20,g21)
    c: Coincident(g21,g-8)
    c: Coincident(g21,g22)
    c: Coincident(g22,g-7)
    c: Coincident(g22,g23)
    c: Coincident(g23,g-7)
    c: Coincident(g23,g24)
    c: Coincident(g24,g-6)
    c: Coincident(g24,g25)
    c: Coincident(g25,g4)
    c: PointOnObject(g27,g29)
    c: Vertical(g27)
    c: PointOnObject(g28,g30)
    c: Vertical(g28)
    c: PointOnObject(g29,g27)
    c: Coincident(g1,g27)
    c: PointOnObject(g30,g28)
    c: Horizontal(g29)
    c: Coincident(g31,g16)
    c: Coincident(g31,g28)
    c: Horizontal(g31)
    c: Horizontal(g30)
    c: Distance(g31,g31) = 2
    c: Tangent(g1,g-19) = -1.5708
    c: DistanceX(g29,g29) = 26
    c: Coincident(g26,g12)
    c: Coincident(g2,g3)
FEATURE [PartDesign::Pad] Pad011  label="ClipRingPad"
  Direction = (0,-1,2e-16)
  Length = 2.6
  Length2 = 10
  Profile = -> Sketch012
  ReferenceAxis = -> Sketch012 [N_Axis]
  Suppressed = false
  Type = 0
FEATURE [Sketcher::SketchObject] Sketch013
  ArcFitTolerance = 1e-06
  AttachmentSupport = -> [Pad011]
  ExternalGeometry = -> [Pad011]
  FullyConstrained = true
  MakeInternals = false
  MapMode = 5
  Placement = pos=(0,-8.1,0) rot=(1,0,0;1.5708rad)
  sketch-geometry (8):
    g0: LineSegment StartX=-61.4 StartY=34 StartZ=0 EndX=-61.4 EndY=-34 EndZ=0
    g1: LineSegment StartX=-61.4 StartY=-34 StartZ=0 EndX=61.6 EndY=-34 EndZ=0
    g2: LineSegment StartX=61.6 StartY=-34 StartZ=0 EndX=61.6 EndY=34 EndZ=0
    g3: LineSegment StartX=61.6 StartY=34 StartZ=0 EndX=-61.4 EndY=34 EndZ=0
    g4: LineSegment StartX=-59.4 StartY=32 StartZ=0 EndX=-59.4 EndY=-32 EndZ=0
    g5: LineSegment StartX=-59.4 StartY=-32 StartZ=0 EndX=59.6 EndY=-32 EndZ=0
    g6: LineSegment StartX=59.6 StartY=-32 StartZ=0 EndX=59.6 EndY=32 EndZ=0
    g7: LineSegment StartX=59.6 StartY=32 StartZ=0 EndX=-59.4 EndY=32 EndZ=0
  constraints (20):
    c: Coincident(g0,g1)
    c: Coincident(g1,g2)
    c: Coincident(g2,g3)
    c: Coincident(g3,g0)
    c: Vertical(g0)
    c: Vertical(g2)
    c: Horizontal(g1)
    c: Horizontal(g3)
    c: Coincident(g0,g-4)
    c: Coincident(g1,g-3)
    c: Coincident(g4,g5)
    c: Coincident(g5,g6)
    c: Coincident(g6,g7)
    c: Coincident(g7,g4)
    c: Vertical(g4)
    c: Vertical(g6)
    c: Horizontal(g5)
    c: Horizontal(g7)
    c: Coincident(g4,g-6)
    c: Coincident(g5,g-5)
FEATURE [PartDesign::Pad] Pad012  label="WholeRingPad"
  BaseFeature = -> Pad011
  Direction = (0,-1,2e-16)
  Length = 0.5
  Length2 = 10
  Profile = -> Sketch013
  ReferenceAxis = -> Sketch013 [N_Axis]
  Suppressed = false
  Type = 0
FEATURE [Sketcher::SketchObject] Sketch014
  ArcFitTolerance = 1e-06
  AttachmentSupport = -> [Pad012]
  ExternalGeometry = -> [Pad012]
  FullyConstrained = true
  MakeInternals = false
  MapMode = 5
  Placement = pos=(0,-7.5e-15,-34) rot=(1,0,0;3.14159rad)
  sketch-geometry (4):
    g0: LineSegment StartX=5.6 StartY=5.5 StartZ=0 EndX=5.6 EndY=8 EndZ=0
    g1: LineSegment StartX=5.6 StartY=8 StartZ=0 EndX=-10.4 EndY=8 EndZ=0
    g2: LineSegment StartX=-10.4 StartY=8 StartZ=0 EndX=-10.4 EndY=5.5 EndZ=0
    g3: LineSegment StartX=-10.4 StartY=5.5 StartZ=0 EndX=5.6 EndY=5.5 EndZ=0
  constraints (12):
    c: Coincident(g0,g1)
    c: Coincident(g1,g2)
    c: Coincident(g2,g3)
    c: Coincident(g3,g0)
    c: Vertical(g0)
    c: Vertical(g2)
    c: Horizontal(g1)
    c: Horizontal(g3)
    c: Distance(g0,g2) = 16
    c: Distance(g1,g3) = 2.5
    c: PointOnObject(g0,g-3)
    c: Distance(g-3,g2) = 8
FEATURE [PartDesign::Pocket] Pocket  label="SDPocket"
  BaseFeature = -> Pad012
  Direction = (0,0,1)
  Length = 5
  Length2 = 5
  Profile = -> Sketch014
  ReferenceAxis = -> Sketch014 [N_Axis]
  Suppressed = false
  Type = 2
FEATURE [Sketcher::SketchObject] Sketch015
  ArcFitTolerance = 1e-06
  AttachmentSupport = -> [Pocket]
  ExternalGeometry = -> [Pocket]
  FullyConstrained = true
  MakeInternals = false
  MapMode = 5
  Placement = pos=(0,-8.1,0) rot=(0,0.707107,0.707107;3.14159rad)
  sketch-geometry (32):
    g0: LineSegment StartX=-34.6 StartY=-34 StartZ=0 EndX=-30.35 EndY=-34 EndZ=0
    g1: ArcOfCircle CenterX=-28.35 CenterY=-34 CenterZ=0 NormalX=0 NormalY=0 NormalZ=1 AngleXU=0 Radius=2 StartAngle=3.14159 EndAngle=6.28319
    g2: LineSegment StartX=-34.6 StartY=-34 StartZ=0 EndX=-34.6 EndY=-32 EndZ=0
    g3: LineSegment StartX=-29.85 StartY=-32.75 StartZ=0 EndX=-29.85 EndY=-31.75 EndZ=0
    g4: LineSegment StartX=-29.85 StartY=-31.75 StartZ=0 EndX=-26.85 EndY=-31.75 EndZ=0
    g5: LineSegment StartX=-26.85 StartY=-31.75 StartZ=0 EndX=-26.85 EndY=-32.75 EndZ=0
    g6: LineSegment StartX=-26.85 StartY=-32.75 StartZ=0 EndX=-20.35 EndY=-32.75 EndZ=0
    g7: LineSegment StartX=-20.35 StartY=-32.75 StartZ=0 EndX=-20.35 EndY=-31.75 EndZ=0
    g8: LineSegment StartX=-20.35 StartY=-31.75 StartZ=0 EndX=-17.35 EndY=-31.75 EndZ=0
    g9: LineSegment StartX=-17.35 StartY=-31.75 StartZ=0 EndX=-17.35 EndY=-32.75 EndZ=0
    g10: LineSegment StartX=-11.85 StartY=-32.75 StartZ=0 EndX=-11.85 EndY=-31.75 EndZ=0
    g11: LineSegment StartX=-11.85 StartY=-31.75 StartZ=0 EndX=-8.85 EndY=-31.75 EndZ=0
    g12: LineSegment StartX=-8.85 StartY=-31.75 StartZ=0 EndX=-8.85 EndY=-32.75 EndZ=0
    g13: LineSegment StartX=-8.85 StartY=-32.75 StartZ=0 EndX=-7.85 EndY=-32.75 EndZ=0
    g14: LineSegment StartX=-7.85 StartY=-32.75 StartZ=0 EndX=-7.85 EndY=-34 EndZ=0
    g15: LineSegment StartX=-7.85 StartY=-34 StartZ=0 EndX=-8.35 EndY=-34 EndZ=0
    g16: LineSegment StartX=-26.35 StartY=-34 StartZ=0 EndX=-20.85 EndY=-34 EndZ=0
    g17: ArcOfCircle CenterX=-18.85 CenterY=-34 CenterZ=0 NormalX=0 NormalY=0 NormalZ=1 AngleXU=0 Radius=2 StartAngle=3.14159 EndAngle=6.28319
    g18: ArcOfCircle CenterX=-10.35 CenterY=-34 CenterZ=0 NormalX=0 NormalY=0 NormalZ=1 AngleXU=0 Radius=2 StartAngle=3.14159 EndAngle=6.28319
    g19: LineSegment StartX=-16.85 StartY=-34 StartZ=0 EndX=-12.35 EndY=-34 EndZ=0
    g20: ArcOfCircle CenterX=-33.85 CenterY=-32 CenterZ=0 NormalX=0 NormalY=0 NormalZ=1 AngleXU=0 Radius=0.75 StartAngle=3.14159 EndAngle=4.71239
    g21: LineSegment StartX=-29.85 StartY=-32.75 StartZ=0 EndX=-33.85 EndY=-32.75 EndZ=0
    g22: GeomPoint X=-28.35 Y=-31.75 Z=0
    g23: GeomPoint X=-18.85 Y=-31.75 Z=0
    g24: GeomPoint X=-10.35 Y=-31.75 Z=0
    g25: LineSegment StartX=-11.85 StartY=-32.75 StartZ=0 EndX=-13.6 EndY=-32.75 EndZ=0
    g26: ArcOfCircle CenterX=-13.6 CenterY=-32.25 CenterZ=0 NormalX=0 NormalY=0 NormalZ=1 AngleXU=0 Radius=0.5 StartAngle=3.14159 EndAngle=4.71239
    g27: LineSegment StartX=-14.1 StartY=-32.25 StartZ=0 EndX=-14.1 EndY=-29.75 EndZ=0
    g28: LineSegment StartX=-14.1 StartY=-29.75 StartZ=0 EndX=-15.1 EndY=-29.75 EndZ=0
    g29: LineSegment StartX=-15.1 StartY=-29.75 StartZ=0 EndX=-15.1 EndY=-32.25 EndZ=0
    g30: ArcOfCircle CenterX=-15.6 CenterY=-32.25 CenterZ=0 NormalX=0 NormalY=0 NormalZ=1 AngleXU=0 Radius=0.5 StartAngle=4.71239 EndAngle=6.28319
    g31: LineSegment StartX=-15.6 StartY=-32.75 StartZ=0 EndX=-17.35 EndY=-32.75 EndZ=0
  constraints (88):
    c: Horizontal(g0)
    c: Coincident(g1,g0)
    c: Horizontal(g0,g1)
    c: Horizontal(g1,g1)
    c: Radius(g1) = 2
    c: Coincident(g0,g2)
    c: Vertical(g3)
    c: Coincident(g3,g4)
    c: Horizontal(g4)
    c: Coincident(g4,g5)
    c: Vertical(g5)
    c: Coincident(g5,g6)
    c: Horizontal(g6)
    c: Coincident(g6,g7)
    c: Vertical(g7)
    c: Coincident(g7,g8)
    c: Horizontal(g8)
    c: Coincident(g8,g9)
    c: Vertical(g9)
    c: Vertical(g10)
    c: Coincident(g10,g11)
    c: Horizontal(g11)
    c: Coincident(g11,g12)
    c: Vertical(g12)
    c: Coincident(g12,g13)
    c: Horizontal(g13)
    c: Coincident(g13,g14)
    c: Vertical(g14)
    c: Coincident(g14,g15)
    c: Horizontal(g15)
    c: Equal(g11,g8)
    c: Equal(g8,g4)
    c: DistanceX(g4,g4) = 3
    c: DistanceX(g6,g6) = 6.5
    c: Horizontal(g3,g5)
    c: Horizontal(g5,g9)
    c: Horizontal(g9,g12)
    c: Horizontal(g10,g8)
    c: Horizontal(g8,g4)
    c: Coincident(g16,g1)
    c: Horizontal(g16)
    c: Coincident(g17,g16)
    c: Coincident(g18,g15)
    c: Coincident(g19,g17)
    c: Coincident(g19,g18)
    c: Horizontal(g19)
    c: Equal(g1,g17)
    c: Equal(g17,g18)
    c: Horizontal(g15,g18)
    c: Horizontal(g18,g18)
    c: Horizontal(g18,g17)
    c: Horizontal(g17,g16)
    c: Coincident(g2,g-3)
    c: Coincident(g21,g3)
    c: Tangent(g21,g20) = 1.5708
    c: Horizontal(g21)
    c: Tangent(g20,g2) = 1.5708
    c: Distance(g0,g21) = 1.25
    c: Symmetric(g4,g4,g22)
    c: Symmetric(g8,g8,g23)
    c: Symmetric(g11,g11,g24)
    c: Vertical(g24,g18)
    c: Vertical(g23,g17)
    c: Vertical(g22,g1)
    c: Coincident(g0,g-3)
    c: Distance(g2,g3) = 4.75
    c: Distance(g15,g15) = 0.5
    c: DistanceY(g3,g3) = 1
    c: Coincident(g10,g25)
    c: Horizontal(g25)
    c: Tangent(g25,g26) = 1.5708
    c: Tangent(g26,g27) = 1.5708
    c: Coincident(g27,g28)
    c: Horizontal(g28)
    c: Coincident(g28,g29)
    c: Vertical(g29)
    c: Tangent(g29,g30) = 1.5708
    c: Coincident(g31,g9)
    c: Horizontal(g31)
    c: Equal(g30,g26)
    c: Equal(g25,g31)
    c: Vertical(g27)
    c: Horizontal(g25,g30)
    c: DistanceX(g9,g10) = 5.5
    c: Radius(g26) = 0.5
    c: DistanceX(g28,g28) = 1
    c: Tangent(g30,g31) = 1.5708
    c: DistanceY(g27,g27) = 2.5
FEATURE [PartDesign::Pad] Pad013  label="ButtonsPad"
  BaseFeature = -> Pocket
  Direction = (0,1,-2e-16)
  Length = 2
  Length2 = -0.4
  Profile = -> Sketch015
  ReferenceAxis = -> Sketch015 [N_Axis]
  Suppressed = false
  Type = 4
FEATURE [Sketcher::SketchObject] Sketch016
  ArcFitTolerance = 1e-06
  AttachmentSupport = -> [Pad010]
  ExternalGeometry = -> [Pad010]
  FullyConstrained = true
  MakeInternals = false
  MapMode = 5
  Placement = pos=(0,-5.5,0) rot=(1,0,0;1.5708rad)
  sketch-geometry (8):
    g0: LineSegment StartX=-10.3 StartY=-34 StartZ=0 EndX=5.5 EndY=-34 EndZ=0
    g1: LineSegment StartX=5.5 StartY=-34 StartZ=0 EndX=5.5 EndY=-32 EndZ=0
    g2: LineSegment StartX=5.5 StartY=-32 StartZ=0 EndX=-10.3 EndY=-32 EndZ=0
    g3: LineSegment StartX=-10.3 StartY=-32 StartZ=0 EndX=-10.3 EndY=-34 EndZ=0
    g4: LineSegment StartX=34.5 StartY=-34 StartZ=0 EndX=34.5 EndY=-32 EndZ=0
    g5: LineSegment StartX=34.5 StartY=-32 StartZ=0 EndX=7.7 EndY=-32 EndZ=0
    g6: LineSegment StartX=7.7 StartY=-32 StartZ=0 EndX=7.7 EndY=-34 EndZ=0
    g7: LineSegment StartX=7.7 StartY=-34 StartZ=0 EndX=34.5 EndY=-34 EndZ=0
  constraints (24):
    c: Coincident(g0,g1)
    c: Coincident(g1,g2)
    c: Coincident(g2,g3)
    c: Coincident(g3,g0)
    c: Horizontal(g0)
    c: Horizontal(g2)
    c: Vertical(g1)
    c: Vertical(g3)
    c: PointOnObject(g0,g-3)
    c: PointOnObject(g1,g-4)
    c: Coincident(g4,g5)
    c: Coincident(g5,g6)
    c: Coincident(g6,g7)
    c: Coincident(g7,g4)
    c: Vertical(g4)
    c: Vertical(g6)
    c: Horizontal(g5)
    c: Horizontal(g7)
    c: PointOnObject(g4,g-3)
    c: PointOnObject(g5,g-4)
    c: DistanceX(g0,g0) = 15.8
    c: DistanceX(g-3,g0) = 8.1
    c: Distance(g-3,g4) = 2.1
    c: DistanceX(g-3,g6) = 26.1
FEATURE [PartDesign::Pad] Pad014  label="SD_ButtonPad"
  BaseFeature = -> Pad010
  Direction = (0,-1,2e-16)
  Length = 0.5
  Length2 = 10
  Placement = pos=(0,0,0) rot=(1,0,0;1.5708rad)
  Profile = -> Sketch016
  ReferenceAxis = -> Sketch016 [N_Axis]
  Suppressed = false
  Type = 0
FEATURE [Sketcher::SketchObject] Sketch017
  ArcFitTolerance = 1e-06
  AttachmentSupport = -> [Pad013]
  ExternalGeometry = -> [Pad013]
  FullyConstrained = true
  MakeInternals = false
  MapMode = 5
  Placement = pos=(-5.68e-14,9e-16,4) rot=(0,0,1;0rad)
  sketch-geometry (2):
    g0: ArcOfCircle CenterX=61.1 CenterY=-7.6 CenterZ=0 NormalX=0 NormalY=0 NormalZ=1 AngleXU=0 Radius=0.5 StartAngle=1.5708 EndAngle=4.71239
    g1: LineSegment StartX=61.1 StartY=-7.1 StartZ=0 EndX=61.1 EndY=-8.1 EndZ=0
  constraints (6):
    c: PointOnObject(g0,g-5)
    c: Coincident(g0,g-5)
    c: PointOnObject(g0,g-5)
    c: Coincident(g1,g0)
    c: Coincident(g1,g0)
    c: DistanceY(g1,g1) = 1
FEATURE [PartDesign::Pocket] Pocket001  label="RightTabPocket"
  BaseFeature = -> Pad013
  Direction = (1.42e-14,0,-1)
  Length = 20
  Length2 = 5
  Profile = -> Sketch017
  ReferenceAxis = -> Sketch017 [N_Axis]
  Reversed = true
  Suppressed = false
  Type = 0
FEATURE [Sketcher::SketchObject] Sketch018
  ArcFitTolerance = 1e-06
  AttachmentSupport = -> [Pocket001]
  ExternalGeometry = -> [Pocket001]
  FullyConstrained = true
  MakeInternals = false
  MapMode = 5
  Placement = pos=(-38.4,0,0) rot=(0.57735,0.57735,0.57735;2.0944rad)
  sketch-geometry (2):
    g0: LineSegment StartX=-8.1 StartY=33.5 StartZ=0 EndX=-7.1 EndY=33.5 EndZ=0
    g1: ArcOfCircle CenterX=-7.6 CenterY=33.5 CenterZ=0 NormalX=0 NormalY=0 NormalZ=1 AngleXU=0 Radius=0.5 StartAngle=3.14159 EndAngle=6.28319
  constraints (6):
    c: Coincident(g0,g-3)
    c: PointOnObject(g0,g-3)
    c: Coincident(g1,g0)
    c: Coincident(g1,g0)
    c: DistanceX(g0,g0) = 1
    c: PointOnObject(g1,g0)
FEATURE [PartDesign::Pocket] Pocket002  label="BotTabPocket"
  BaseFeature = -> Pocket001
  Direction = (-1,0,0)
  Length = 60
  Length2 = 5
  Profile = -> Sketch018
  ReferenceAxis = -> Sketch018 [N_Axis]
  Reversed = true
  Suppressed = false
  Type = 0
FEATURE [Sketcher::SketchObject] Sketch019
  ArcFitTolerance = 1e-06
  AttachmentSupport = -> [Pocket001]
  ExternalGeometry = -> [Pocket001]
  FullyConstrained = true
  MakeInternals = false
  MapMode = 5
  Placement = pos=(-2.274e-13,-3.5e-15,-16) rot=(0,0,1;0rad)
  sketch-geometry (2):
    g0: ArcOfCircle CenterX=-60.9 CenterY=-7.6 CenterZ=0 NormalX=0 NormalY=0 NormalZ=1 AngleXU=0 Radius=0.5 StartAngle=4.71239 EndAngle=7.85398
    g1: LineSegment StartX=-60.9 StartY=-7.1 StartZ=0 EndX=-60.9 EndY=-8.1 EndZ=0
  constraints (6):
    c: PointOnObject(g0,g-3)
    c: Coincident(g0,g-3)
    c: PointOnObject(g0,g-3)
    c: Coincident(g1,g0)
    c: Coincident(g1,g0)
    c: Radius(g0) = 0.5
FEATURE [PartDesign::Pocket] Pocket003  label="LeftTabPocket"
  BaseFeature = -> Pocket002
  Direction = (-1.42e-14,0,-1)
  Length = 30
  Length2 = 5
  Profile = -> Sketch019
  ReferenceAxis = -> Sketch019 [N_Axis]
  Reversed = true
  Suppressed = false
  Type = 0
FEATURE [Sketcher::SketchObject] Sketch020
  ArcFitTolerance = 1e-06
  AttachmentSupport = -> [Pocket003]
  ExternalGeometry = -> [Pocket003]
  FullyConstrained = true
  MakeInternals = false
  MapMode = 5
  Placement = pos=(-18.4,0,0) rot=(0.57735,-0.57735,-0.57735;2.0944rad)
  sketch-geometry (2):
    g0: ArcOfCircle CenterX=7.6 CenterY=-33.5 CenterZ=0 NormalX=0 NormalY=0 NormalZ=1 AngleXU=0 Radius=0.5 StartAngle=1.16e-14 EndAngle=3.14159
    g1: LineSegment StartX=7.1 StartY=-33.5 StartZ=0 EndX=8.1 EndY=-33.5 EndZ=0
  constraints (6):
    c: PointOnObject(g0,g-3)
    c: Coincident(g0,g-3)
    c: PointOnObject(g0,g-3)
    c: Coincident(g1,g0)
    c: Coincident(g1,g0)
    c: DistanceX(g1,g1) = 1
FEATURE [PartDesign::Pocket] Pocket004  label="TopTab1Pocket"
  BaseFeature = -> Pocket003
  Direction = (1,0,0)
  Length = 30
  Length2 = 5
  Profile = -> Sketch020
  ReferenceAxis = -> Sketch020 [N_Axis]
  Reversed = true
  Suppressed = false
  Type = 0
FEATURE [Sketcher::SketchObject] Sketch021
  ArcFitTolerance = 1e-06
  AttachmentSupport = -> [Pocket004]
  ExternalGeometry = -> [Pocket004]
  FullyConstrained = true
  MakeInternals = false
  MapMode = 5
  Placement = pos=(51.6,0,-7.332e-13) rot=(0.57735,-0.57735,-0.57735;2.0944rad)
  sketch-geometry (2):
    g0: LineSegment StartX=8.1 StartY=-33.5 StartZ=0 EndX=7.1 EndY=-33.5 EndZ=0
    g1: ArcOfCircle CenterX=7.6 CenterY=-33.5 CenterZ=0 NormalX=0 NormalY=0 NormalZ=1 AngleXU=0 Radius=0.5 StartAngle=-2.913e-13 EndAngle=3.14159
  constraints (6):
    c: DistanceX(g0,g0) = 1
    c: PointOnObject(g0,g-3)
    c: Coincident(g0,g-3)
    c: Coincident(g1,g0)
    c: Coincident(g1,g0)
    c: PointOnObject(g1,g0)
FEATURE [PartDesign::Pocket] Pocket005  label="TopTab2Pocket"
  BaseFeature = -> Pocket004
  Direction = (1,0,-1.42e-14)
  Length = 15
  Length2 = 5
  Profile = -> Sketch021
  ReferenceAxis = -> Sketch021 [N_Axis]
  Reversed = true
  Suppressed = false
  Type = 0
FEATURE [Sketcher::SketchObject] Sketch022
  ArcFitTolerance = 1e-06
  AttachmentSupport = -> [Pocket005]
  ExternalGeometry = -> [Pocket005]
  FullyConstrained = true
  MakeInternals = false
  MapMode = 5
  Placement = pos=(0,-8.6,0) rot=(1,0,0;1.5708rad)
  sketch-geometry (32):
    g0: LineSegment StartX=59.6 StartY=-32 StartZ=0 EndX=59.6 EndY=-15 EndZ=0
    g1: LineSegment StartX=59.6 StartY=-15 StartZ=0 EndX=54.6 EndY=-15 EndZ=0
    g2: LineSegment StartX=49.6 StartY=-20 StartZ=0 EndX=49.6 EndY=-27 EndZ=0
    g3: Circle CenterX=53.9 CenterY=-26.9 CenterZ=0 NormalX=0 NormalY=0 NormalZ=1 AngleXU=0 Radius=2
    g4: Circle CenterX=53.9 CenterY=-18.7 CenterZ=0 NormalX=0 NormalY=0 NormalZ=1 AngleXU=0 Radius=1.275
    g5: ArcOfCircle CenterX=54.6 CenterY=-20 CenterZ=0 NormalX=0 NormalY=0 NormalZ=1 AngleXU=0 Radius=5 StartAngle=1.5708 EndAngle=3.14159
    g6: GeomPoint [constr] X=49.6 Y=-15 Z=0
    g7: LineSegment StartX=59.6 StartY=-32 StartZ=0 EndX=44.6 EndY=-32 EndZ=0
    g8: ArcOfCircle CenterX=44.6 CenterY=-27 CenterZ=0 NormalX=0 NormalY=0 NormalZ=1 AngleXU=0 Radius=5 StartAngle=4.71239 EndAngle=6.28319
    g9: LineSegment StartX=-39.7 StartY=-32 StartZ=0 EndX=-59.4 EndY=-32 EndZ=0
    g10: LineSegment StartX=-59.4 StartY=-32 StartZ=0 EndX=-59.4 EndY=-24.5 EndZ=0
    g11: ArcOfCircle CenterX=-46.7 CenterY=-26.9 CenterZ=0 NormalX=0 NormalY=0 NormalZ=1 AngleXU=0 Radius=4 StartAngle=0 EndAngle=2.49809
    g12: LineSegment StartX=-42.7 StartY=-26.9 StartZ=0 EndX=-42.7 EndY=-29 EndZ=0
    g13: ArcOfCircle CenterX=-39.7 CenterY=-29 CenterZ=0 NormalX=0 NormalY=0 NormalZ=1 AngleXU=0 Radius=3 StartAngle=3.14159 EndAngle=4.71239
    g14: LineSegment StartX=-59.4 StartY=-24.5 StartZ=0 EndX=-49.9 EndY=-24.5 EndZ=0
    g15: Circle CenterX=-53.9 CenterY=-26.9 CenterZ=0 NormalX=0 NormalY=0 NormalZ=1 AngleXU=0 Radius=1.275
    g16: Circle CenterX=-46.7 CenterY=-26.9 CenterZ=0 NormalX=0 NormalY=0 NormalZ=1 AngleXU=0 Radius=2
    g17: LineSegment StartX=-59.4 StartY=10.1145 StartZ=0 EndX=-59.4 EndY=23.0855 EndZ=0
    g18: LineSegment StartX=-56.6951 StartY=13.1 StartZ=0 EndX=-46.4541 EndY=14.1121 EndZ=0
    g19: LineSegment StartX=-46.4541 StartY=19.0879 StartZ=0 EndX=-56.6951 EndY=20.1 EndZ=0
    g20: ArcOfCircle CenterX=-46.7 CenterY=16.6 CenterZ=0 NormalX=0 NormalY=0 NormalZ=1 AngleXU=0 Radius=2.5 StartAngle=4.8109 EndAngle=7.75547
    g21: Circle CenterX=-46.7 CenterY=16.6 CenterZ=0 NormalX=0 NormalY=0 NormalZ=1 AngleXU=0 Radius=1.275
    g22: Circle CenterX=-53.9 CenterY=16.6 CenterZ=0 NormalX=0 NormalY=0 NormalZ=1 AngleXU=0 Radius=2
    g23: ArcOfCircle CenterX=-56.4 CenterY=10.1145 CenterZ=0 NormalX=0 NormalY=0 NormalZ=1 AngleXU=0 Radius=3 StartAngle=1.66931 EndAngle=3.14159
    g24: ArcOfCircle CenterX=-56.4 CenterY=23.0855 CenterZ=0 NormalX=0 NormalY=0 NormalZ=1 AngleXU=0 Radius=3 StartAngle=3.14159 EndAngle=4.61388
    g25: GeomPoint X=-59.4 Y=16.6 Z=0
    g26: LineSegment StartX=59.6 StartY=32 StartZ=0 EndX=51 EndY=32 EndZ=0
    g27: LineSegment StartX=51 StartY=32 StartZ=0 EndX=51 EndY=26.9 EndZ=0
    g28: ArcOfCircle CenterX=53.9 CenterY=26.9 CenterZ=0 NormalX=0 NormalY=0 NormalZ=1 AngleXU=0 Radius=2.9 StartAngle=3.14159 EndAngle=4.71239
    g29: LineSegment StartX=53.9 StartY=24 StartZ=0 EndX=59.6 EndY=24 EndZ=0
    g30: LineSegment StartX=59.6 StartY=24 StartZ=0 EndX=59.6 EndY=32 EndZ=0
    g31: Circle CenterX=53.9 CenterY=26.9 CenterZ=0 NormalX=0 NormalY=0 NormalZ=1 AngleXU=0 Radius=1.275
  constraints (80):
    c: Coincident(g0,g1)
    c: Vertical(g0)
    c: Vertical(g2)
    c: Horizontal(g1)
    c: Distance(g1,g0) = 17
    c: Coincident(g0,g-4)
    c: Vertical(g4,g3)
    c: PointOnObject(g6,g1)
    c: PointOnObject(g6,g2)
    c: Tangent(g1,g5) = -1.5708
    c: Tangent(g2,g5) = -1.5708
    c: Distance(g3,g0) = 5.7
    c: Radius(g5) = 5
    c: Diameter(g4) = 2.55
    c: Diameter(g3) = 4
    c: Coincident(g7,g0)
    c: PointOnObject(g7,g-3)
    c: Tangent(g8,g7) = 1.5708
    c: Tangent(g2,g8) = 1.5708
    c: Radius(g8) = 5
    c: Distance(g2,g0) = 10
    c: Distance(g3,g7) = 5.1
    c: Distance(g4,g7) = 13.3
    c: PointOnObject(g9,g-3)
    c: Coincident(g9,g-6)
    c: Coincident(g9,g10)
    c: PointOnObject(g10,g-6)
    c: Vertical(g12)
    c: Tangent(g12,g13) = -1.5708
    c: Tangent(g13,g9) = 1.5708
    c: Distance(g10,g9) = 7.5
    c: Tangent(g11,g12) = 1.5708
    c: Radius(g11) = 4
    c: Radius(g13) = 3
    c: Coincident(g14,g10)
    c: Horizontal(g14)
    c: Coincident(g11,g14)
    c: Diameter(g15) = 2.55
    c: Diameter(g16) = 4
    c: Coincident(g16,g11)
    c: Horizontal(g15,g11)
    c: Distance(g15,g10) = 5.5
    c: Distance(g11,g10) = 12.7
    c: Distance(g15,g9) = 5.1
    c: PointOnObject(g17,g-6)
    c: PointOnObject(g17,g-6)
    c: Vertical(g18,g19)
    c: Tangent(g20,g18) = -1.5708
    c: Tangent(g20,g19) = -1.5708
    c: Coincident(g21,g20)
    c: Horizontal(g20,g22)
    c: Tangent(g24,g19) = 1.5708
    c: Tangent(g23,g18) = 1.5708
    c: Tangent(g23,g17) = 1.5708
    c: Tangent(g24,g17) = 1.5708
    c: Diameter(g22) = 4
    c: Diameter(g21) = 2.55
    c: Radius(g20) = 2.5
    c: Distance(g22,g17) = 5.5
    c: Distance(g20,g17) = 12.7
    c: Distance(g22,g-5) = 15.4
    c: Radius(g23) = 3
    c: DistanceY(g18,g19) = 7
    c: Symmetric(g17,g17,g25)
    c: Horizontal(g25,g22)
    c: Coincident(g-5,g26)
    c: PointOnObject(g26,g-5)
    c: Coincident(g26,g27)
    c: Vertical(g27)
    c: Tangent(g27,g28) = -1.5708
    c: Tangent(g28,g29) = -1.5708
    c: Coincident(g29,g30)
    c: Coincident(g30,g26)
    c: Vertical(g30)
    c: Horizontal(g29)
    c: Diameter(g31) = 2.55
    c: Distance(g31,g30) = 5.7
    c: Distance(g31,g26) = 5.1
    c: DistanceY(g30,g30) = 8
    c: Coincident(g28,g31)
FEATURE [PartDesign::Pad] Pad015  label="ScrewPad"
  BaseFeature = -> Pocket005
  Direction = (0,-1,2e-16)
  Length = 2.6
  Length2 = 10
  Profile = -> Sketch022
  ReferenceAxis = -> Sketch022 [N_Axis]
  Reversed = true
  Suppressed = false
  Type = 0
FEATURE [Sketcher::SketchObject] Sketch023
  ArcFitTolerance = 1e-06
  AttachmentSupport = -> [Pad015]
  ExternalGeometry = -> [Pad015]
  FullyConstrained = true
  MakeInternals = false
  MapMode = 5
  Placement = pos=(61.6,0,0) rot=(0.57735,0.57735,0.57735;2.0944rad)
  sketch-geometry (10):
    g0: ArcOfCircle CenterX=-8.6 CenterY=-30 CenterZ=0 NormalX=0 NormalY=0 NormalZ=1 AngleXU=0 Radius=4 StartAngle=3.63414 EndAngle=4.71239
    g1: LineSegment StartX=-12.1245 StartY=-31.8915 StartZ=0 EndX=-38.9472 EndY=18.0891 EndZ=0
    g2: ArcOfCircle CenterX=-35.4227 CenterY=19.9806 CenterZ=0 NormalX=0 NormalY=0 NormalZ=1 AngleXU=0 Radius=4 StartAngle=1.91986 EndAngle=3.63414
    g3: LineSegment StartX=-36.7908 StartY=23.7394 StartZ=0 EndX=-8.6 EndY=34 EndZ=0
    g4: LineSegment StartX=-8.6 StartY=31.8716 StartZ=0 EndX=-36.1067 EndY=21.86 EndZ=0
    g5: ArcOfCircle CenterX=-35.4227 CenterY=19.9806 CenterZ=0 NormalX=0 NormalY=0 NormalZ=1 AngleXU=0 Radius=2 StartAngle=1.91986 EndAngle=3.63414
    g6: LineSegment StartX=-37.185 StartY=19.0349 StartZ=0 EndX=-10.3623 EndY=-30.9457 EndZ=0
    g7: ArcOfCircle CenterX=-8.6 CenterY=-30 CenterZ=0 NormalX=0 NormalY=0 NormalZ=1 AngleXU=0 Radius=2 StartAngle=3.63414 EndAngle=4.71239
    g8: LineSegment StartX=-8.6 StartY=-32 StartZ=0 EndX=-8.6 EndY=-34 EndZ=0
    g9: LineSegment StartX=-8.6 StartY=31.8716 StartZ=0 EndX=-8.6 EndY=34 EndZ=0
  constraints (24):
    c: PointOnObject(g0,g-3)
    c: Coincident(g0,g-3)
    c: Tangent(g1,g2) = 1.5708
    c: Coincident(g3,g-3)
    c: Tangent(g2,g3) = 1.5708
    c: Tangent(g0,g1) = 1.5708
    c: Angle(g3,g-3) = 1.22173
    c: PointOnObject(g4,g-3)
    c: Tangent(g4,g5) = -1.5708
    c: Tangent(g6,g7) = -1.5708
    c: PointOnObject(g7,g-3)
    c: Coincident(g8,g7)
    c: Coincident(g8,g0)
    c: Coincident(g9,g4)
    c: Coincident(g9,g3)
    c: Tangent(g5,g6) = -1.5708
    c: Coincident(g7,g0)
    c: Coincident(g5,g2)
    c: Distance(g4,g3) = 2
    c: Parallel(g3,g4)
    c: Parallel(g6,g1)
    c: Distance(g3,g3) = 30
    c: Radius(g7) = 2
    c: Radius(g2) = 4
FEATURE [PartDesign::Pad] Pad016  label="BackShellPad"
  BaseFeature = -> Pad015
  Direction = (1,0,0)
  Length = 10
  Length2 = 10
  Profile = -> Sketch023
  ReferenceAxis = -> Sketch023 [N_Axis]
  Reversed = true
  Suppressed = false
  Type = 3
  UpToFace = -> Pad015 [Face30]
FEATURE [Sketcher::SketchObject] Sketch024
  ArcFitTolerance = 1e-06
  AttachmentSupport = -> [Pad016]
  ExternalGeometry = -> [Pad016]
  FullyConstrained = true
  MakeInternals = false
  MapMode = 5
  Placement = pos=(61.6,0,0) rot=(0.57735,0.57735,0.57735;2.0944rad)
  sketch-geometry (5):
    g0: LineSegment StartX=-36.7908 StartY=23.7394 StartZ=0 EndX=-8.6 EndY=34 EndZ=0
    g1: LineSegment StartX=-8.6 StartY=34 StartZ=0 EndX=-8.6 EndY=-34 EndZ=0
    g2: LineSegment StartX=-12.1245 StartY=-31.8915 StartZ=0 EndX=-38.9472 EndY=18.0891 EndZ=0
    g3: ArcOfCircle CenterX=-35.4227 CenterY=19.9806 CenterZ=0 NormalX=0 NormalY=0 NormalZ=1 AngleXU=0 Radius=4 StartAngle=1.91986 EndAngle=3.63414
    g4: ArcOfCircle CenterX=-8.6 CenterY=-30 CenterZ=0 NormalX=0 NormalY=0 NormalZ=1 AngleXU=0 Radius=4 StartAngle=3.63414 EndAngle=4.71239
  constraints (12):
    c: Coincident(g-5,g0)
    c: Coincident(g0,g-5)
    c: Coincident(g0,g1)
    c: Coincident(g1,g-3)
    c: Coincident(g2,g-3)
    c: Coincident(g2,g-4)
    c: Coincident(g3,g-4)
    c: Coincident(g3,g2)
    c: Horizontal(g3,g0)
    c: Vertical(g4,g1)
    c: Coincident(g4,g2)
    c: Coincident(g4,g-3)
FEATURE [PartDesign::Pad] Pad017  label="RightSidePad"
  BaseFeature = -> Pad016
  Direction = (1,0,0)
  Length = 2
  Length2 = 10
  Profile = -> Sketch024
  ReferenceAxis = -> Sketch024 [N_Axis]
  Reversed = true
  Suppressed = false
  Type = 0
FEATURE [PartDesign::LinearPattern] LinearPattern  label="LeftSideLinearPattern"
  BaseFeature = -> Pad017
  Direction = -> X_Axis006
  Length = 121
  Mode = 1
  Occurrences = 2
  Offset = 121
  Originals = -> [Pad017]
  Reversed = true
  Suppressed = false
  TransformMode = 0
FEATURE [Sketcher::SketchObject] Sketch025
  ArcFitTolerance = 1e-06
  AttachmentSupport = -> [Pad015]
  FullyConstrained = true
  MakeInternals = false
  MapMode = 5
  Placement = pos=(61.6,0,0) rot=(0.57735,0.57735,0.57735;2.0944rad)
  expr: Constraints[7] = 10 - 5.5
  sketch-geometry (6):
    g0: ArcOfCircle CenterX=-7.6 CenterY=-10.05 CenterZ=0 NormalX=0 NormalY=0 NormalZ=1 AngleXU=0 Radius=2.8 StartAngle=3.14159 EndAngle=6.28319
    g1: ArcOfCircle CenterX=-7.6 CenterY=-5.55 CenterZ=0 NormalX=0 NormalY=0 NormalZ=1 AngleXU=0 Radius=2.8 StartAngle=1e-16 EndAngle=3.14159
    g2: LineSegment StartX=-10.4 StartY=-10.05 StartZ=0 EndX=-10.4 EndY=-5.55 EndZ=0
    g3: LineSegment StartX=-4.8 StartY=-10.05 StartZ=0 EndX=-4.8 EndY=-5.55 EndZ=0
    g4: LineSegment [constr] StartX=-7.6 StartY=-10.05 StartZ=0 EndX=-7.6 EndY=-5.55 EndZ=0
    g5: GeomPoint [constr] X=-7.6 Y=-7.8 Z=0
  constraints (13):
    c: Tangent(g0,g2) = 1.5708
    c: Tangent(g0,g3) = -1.5708
    c: Tangent(g1,g2) = 1.5708
    c: Tangent(g1,g3) = -1.5708
    c: Equal(g0,g1)
    c: Vertical(g3)
    c: Distance(g2,g3) = 5.6
    c: DistanceY(g0,g1) = 4.5
    c: Coincident(g4,g0)
    c: Coincident(g4,g1)
    c: Symmetric(g4,g4,g5)
    c: DistanceX(g5,g-1) = 7.6
    c: Distance(g5,g-1) = 7.8
FEATURE [PartDesign::Pocket] Pocket006  label="USBPocket"
  BaseFeature = -> LinearPattern
  Direction = (-1,0,0)
  Length = 5
  Length2 = 5
  Profile = -> Sketch025
  ReferenceAxis = -> Sketch025 [N_Axis]
  Suppressed = false
  Type = 2
FEATURE [Sketcher::SketchObject] Sketch026
  ArcFitTolerance = 1e-06
  AttachmentSupport = -> [Pad016]
  FullyConstrained = false
  MakeInternals = false
  MapMode = 5
  Placement = pos=(0,-22.7013,-12.1829) rot=(1,0,0;2.06334rad)
  sketch-geometry (28):
    g0: ArcOfCircle CenterX=-20 CenterY=0 CenterZ=0 NormalX=0 NormalY=0 NormalZ=1 AngleXU=0 Radius=0.5 StartAngle=9.1405e-12 EndAngle=3.14159
    g1: ArcOfCircle CenterX=-20 CenterY=-15 CenterZ=0 NormalX=0 NormalY=0 NormalZ=1 AngleXU=0 Radius=0.5 StartAngle=3.14159 EndAngle=6.28319
    g2: LineSegment StartX=-19.5 StartY=4.5702e-12 StartZ=0 EndX=-19.5 EndY=-15 EndZ=0
    g3: LineSegment StartX=-20.5 StartY=-2.48e-13 StartZ=0 EndX=-20.5 EndY=-15 EndZ=0
    g4: ArcOfCircle CenterX=-22.5 CenterY=0 CenterZ=0 NormalX=0 NormalY=0 NormalZ=1 AngleXU=0 Radius=0.5 StartAngle=1.6e-15 EndAngle=3.14159
    g5: ArcOfCircle CenterX=-22.5 CenterY=-15 CenterZ=0 NormalX=0 NormalY=0 NormalZ=1 AngleXU=0 Radius=0.5 StartAngle=3.14159 EndAngle=6.28319
    g6: LineSegment StartX=-22 StartY=8e-16 StartZ=0 EndX=-22 EndY=-15 EndZ=0
    g7: LineSegment StartX=-23 StartY=1e-16 StartZ=0 EndX=-23 EndY=-15 EndZ=0
    g8: ArcOfCircle CenterX=-25 CenterY=-1.73205e-07 CenterZ=0 NormalX=0 NormalY=0 NormalZ=1 AngleXU=0 Radius=0.5 StartAngle=1.6e-15 EndAngle=3.14159
    g9: ArcOfCircle CenterX=-25 CenterY=-15 CenterZ=0 NormalX=0 NormalY=0 NormalZ=1 AngleXU=0 Radius=0.5 StartAngle=3.14159 EndAngle=6.28319
    g10: LineSegment StartX=-24.5 StartY=-1.73205e-07 StartZ=0 EndX=-24.5 EndY=-15 EndZ=0
    g11: LineSegment StartX=-25.5 StartY=-1.73205e-07 StartZ=0 EndX=-25.5 EndY=-15 EndZ=0
    g12: ArcOfCircle CenterX=-27.5 CenterY=0 CenterZ=0 NormalX=0 NormalY=0 NormalZ=1 AngleXU=0 Radius=0.5 StartAngle=1.6e-15 EndAngle=3.14159
    g13: ArcOfCircle CenterX=-27.5 CenterY=-15 CenterZ=0 NormalX=0 NormalY=0 NormalZ=1 AngleXU=0 Radius=0.5 StartAngle=3.14159 EndAngle=6.28319
    g14: LineSegment StartX=-27 StartY=8e-16 StartZ=0 EndX=-27 EndY=-15 EndZ=0
    g15: LineSegment StartX=-28 StartY=1e-16 StartZ=0 EndX=-28 EndY=-15 EndZ=0
    g16: ArcOfCircle CenterX=-30 CenterY=0 CenterZ=0 NormalX=0 NormalY=0 NormalZ=1 AngleXU=0 Radius=0.5 StartAngle=1.6e-15 EndAngle=3.14159
    g17: ArcOfCircle CenterX=-30 CenterY=-15 CenterZ=0 NormalX=0 NormalY=0 NormalZ=1 AngleXU=0 Radius=0.5 StartAngle=3.14159 EndAngle=6.28319
    g18: LineSegment StartX=-29.5 StartY=8e-16 StartZ=0 EndX=-29.5 EndY=-15 EndZ=0
    g19: LineSegment StartX=-30.5 StartY=1e-16 StartZ=0 EndX=-30.5 EndY=-15 EndZ=0
    g20: ArcOfCircle CenterX=-32.5 CenterY=-9e-16 CenterZ=0 NormalX=0 NormalY=0 NormalZ=1 AngleXU=0 Radius=0.5 StartAngle=1.8e-15 EndAngle=3.14159
    g21: ArcOfCircle CenterX=-32.5 CenterY=-15 CenterZ=0 NormalX=0 NormalY=0 NormalZ=1 AngleXU=0 Radius=0.5 StartAngle=3.14159 EndAngle=6.28319
    g22: LineSegment StartX=-32 StartY=0 StartZ=0 EndX=-32 EndY=-15 EndZ=0
    g23: LineSegment StartX=-33 StartY=-8e-16 StartZ=0 EndX=-33 EndY=-15 EndZ=0
    g24: ArcOfCircle CenterX=-35 CenterY=0 CenterZ=0 NormalX=0 NormalY=0 NormalZ=1 AngleXU=0 Radius=0.5 StartAngle=1.8e-15 EndAngle=3.14159
    g25: ArcOfCircle CenterX=-35 CenterY=-15 CenterZ=0 NormalX=0 NormalY=0 NormalZ=1 AngleXU=0 Radius=0.5 StartAngle=3.14159 EndAngle=6.28319
    g26: LineSegment StartX=-34.5 StartY=9e-16 StartZ=0 EndX=-34.5 EndY=-15 EndZ=0
    g27: LineSegment StartX=-35.5 StartY=1e-16 StartZ=0 EndX=-35.5 EndY=-15 EndZ=0
  constraints (58):
    c: Tangent(g0,g2) = 1.5708
    c: Tangent(g0,g3) = -1.5708
    c: Tangent(g1,g2) = 1.5708
    c: Tangent(g1,g3) = -1.5708
    c: Equal(g0,g1)
    c: Vertical(g3)
    c: Distance(g0,g1) = 15
    c: Radius(g0) = 0.5
    c: PointOnObject(g0,g-1)
    c: DistanceX(g0,g-1) = 20
    c: Tangent(g4,g6) = 1.5708
    c: Tangent(g8,g10) = 1.5708
    c: Tangent(g12,g14) = 1.5708
    c: Tangent(g16,g18) = 1.5708
    c: Tangent(g20,g22) = 1.5708
    c: Tangent(g24,g26) = 1.5708
    c: Tangent(g4,g7) = -1.5708
    c: Tangent(g8,g11) = -1.5708
    c: Tangent(g12,g15) = -1.5708
    c: Tangent(g16,g19) = -1.5708
    c: Tangent(g20,g23) = -1.5708
    c: Tangent(g24,g27) = -1.5708
    c: Tangent(g5,g6) = 1.5708
    c: Tangent(g9,g10) = 1.5708
    c: Tangent(g13,g14) = 1.5708
    c: Tangent(g17,g18) = 1.5708
    c: Tangent(g21,g22) = 1.5708
    c: Tangent(g25,g26) = 1.5708
    c: Tangent(g5,g7) = -1.5708
    c: Tangent(g9,g11) = -1.5708
    c: Tangent(g13,g15) = -1.5708
    c: Tangent(g17,g19) = -1.5708
    c: Tangent(g21,g23) = -1.5708
    c: Tangent(g25,g27) = -1.5708
    c: Equal(g4,g5)
    c: Equal(g8,g9)
    c: Equal(g12,g13)
    c: Equal(g16,g17)
    c: Equal(g20,g21)
    c: Equal(g24,g25)
    c: Vertical(g7)
    c: Vertical(g11)
    c: Vertical(g15)
    c: Vertical(g19)
    c: Vertical(g23)
    c: Vertical(g27)
    c: Distance(g4,g5) = 15
    c: Distance(g8,g9) = 15
    c: Distance(g12,g13) = 15
    c: Distance(g16,g17) = 15
    c: Distance(g20,g21) = 15
    c: Distance(g24,g25) = 15
    c: Radius(g4) = 0.5
    c: Radius(g8) = 0.5
    c: Radius(g12) = 0.5
    c: Radius(g16) = 0.5
    c: Radius(g20) = 0.5
    c: Radius(g24) = 0.5
FEATURE [PartDesign::Pocket] Pocket007  label="VentPocket"
  BaseFeature = -> Pocket006
  Direction = (0,0.881132,0.47287)
  Length = 5
  Length2 = 5
  Profile = -> Sketch026
  ReferenceAxis = -> Sketch026 [N_Axis]
  Suppressed = false
  Type = 2
FEATURE [PartDesign::Fillet] Fillet
  Base = -> Pad014 [Edge5,Edge8,Edge2,Edge1]
  BaseFeature = -> Pad014
  Placement = pos=(0,0,0) rot=(1,0,0;1.5708rad)
  Radius = 2
  SupportTransform = false
  Suppressed = false
  UseAllEdges = false
FEATURE [PartDesign::Chamfer] Chamfer
  Angle = 45
  Base = -> Fillet [Edge15,Edge12,Edge14,Edge13]
  BaseFeature = -> Fillet
  ChamferType = 0
  FlipDirection = false
  Placement = pos=(0,0,0) rot=(1,0,0;1.5708rad)
  Size = 1.6
  Size2 = 1
  SupportTransform = false
  Suppressed = false
  UseAllEdges = false
FEATURE [PartDesign::Body] Body  label="FaceBody"
  AllowCompound = false
  Group = -> [Sketch,Pad,Sketch001,Pad001,Sketch008,Pad006,Sketch009,Pad007,Sketch010,Pad008,Sketch011,Pad009,Pad010,Sketch016,Pad014,Fillet,Chamfer]
  Origin = -> Origin002
  Tip = -> Chamfer
FEATURE [Sketcher::SketchObject] Sketch027
  ArcFitTolerance = 1e-06
  AttachmentSupport = -> [YZ_Plane006]
  ExternalGeometry = -> [Pocket007]
  FullyConstrained = true
  MakeInternals = false
  MapMode = 5
  Placement = pos=(0,0,0) rot=(0.57735,0.57735,0.57735;2.0944rad)
  sketch-geometry (9):
    g0: GeomPoint [constr] X=-25.2416 Y=16.0242 Z=0
    g1: ArcOfCircle CenterX=-25.2416 CenterY=16.0242 CenterZ=0 NormalX=0 NormalY=0 NormalZ=1 AngleXU=0 Radius=9.2 StartAngle=0.740423 EndAngle=1.91986
    g2: ArcOfCircle CenterX=-18.0812 CenterY=22.5678 CenterZ=0 NormalX=0 NormalY=0 NormalZ=1 AngleXU=0 Radius=0.5 StartAngle=3.88202 EndAngle=6.63225
    g3: LineSegment StartX=-17.6114 StartY=22.7388 StartZ=0 EndX=-19.4925 EndY=27.9071 EndZ=0
    g4: LineSegment StartX=-19.4925 StartY=27.9071 StartZ=0 EndX=-28.3882 EndY=24.6693 EndZ=0
    g5: LineSegment StartX=-32.6202 StartY=10.5291 StartZ=0 EndX=-28.6659 EndY=3.16077 EndZ=0
    g6: LineSegment StartX=-28.6659 StartY=3.16077 StartZ=0 EndX=-23.3162 EndY=6.03177 EndZ=0
    g7: ArcOfCircle CenterX=-25.2416 CenterY=16.0242 CenterZ=0 NormalX=0 NormalY=0 NormalZ=1 AngleXU=0 Radius=9.2 StartAngle=3.78171 EndAngle=4.8874
    g8: ArcOfCircle CenterX=-23.5526 CenterY=6.47233 CenterZ=0 NormalX=0 NormalY=0 NormalZ=1 AngleXU=0 Radius=0.5 StartAngle=5.20493 EndAngle=8.02899
  constraints (23):
    c: Coincident(g1,g0)
    c: PointOnObject(g1,g-3)
    c: PointOnObject(g3,g-3)
    c: Coincident(g4,g3)
    c: Tangent(g4,g1) = -1.5708
    c: Radius(g1) = 9.2
    c: Radius(g2) = 0.5
    c: Distance(g0,g-4) = 9.1
    c: Tangent(g2,g1) = 1.5708
    c: Tangent(g3,g2) = -1.5708
    c: Perpendicular(g-3,g3)
    c: Distance(g3,g3) = 5.5
    c: PointOnObject(g5,g-4)
    c: PointOnObject(g5,g-4)
    c: Coincident(g6,g5)
    c: Coincident(g7,g0)
    c: Coincident(g7,g5)
    c: Perpendicular(g5,g6)
    c: Equal(g8,g2)
    c: Equal(g1,g7)
    c: Tangent(g6,g8) = -1.5708
    c: Tangent(g8,g7) = 1.5708
    c: Distance(g8,g2) = 16
FEATURE [PartDesign::Pad] Pad018
  BaseFeature = -> Pocket007
  Direction = (1,0,0)
  Length = 50
  Length2 = 10
  Midplane = true
  Profile = -> Sketch027
  ReferenceAxis = -> Sketch027 [N_Axis]
  Suppressed = false
  Type = 0
FEATURE [PartDesign::Pad] Pad019
  BaseFeature = -> Pad018
  Direction = (0,-1,0)
  Length = 3
  Length2 = 10
  Profile = -> Pad018 [Face45,Face48,Face90,Face96]
  Suppressed = false
  Type = 0
FEATURE [PartDesign::Body] Body003  label="BackBody"
  AllowCompound = false
  Group = -> [Binder,Sketch012,Pad011,Sketch013,Pad012,Sketch014,Pocket,Sketch015,Pad013,Sketch017,Pocket001,Sketch018,Pocket002,Sketch019,Pocket003,Sketch020,Pocket004,Sketch021,Pocket005,Sketch022,Pad015,Sketch023,Pad016,Sketch024,Pad017,LinearPattern,Sketch025,Pocket006,Sketch026,Pocket007,Sketch027,Pad018,Pad019]
  Origin = -> Origin006
  Tip = -> Pad019
FEATURE [App::Part] Part
  Group = -> [Body,Body003]
  Origin = -> Origin001
  Placement = pos=(0,6,0) rot=(0,0,1;0rad)
